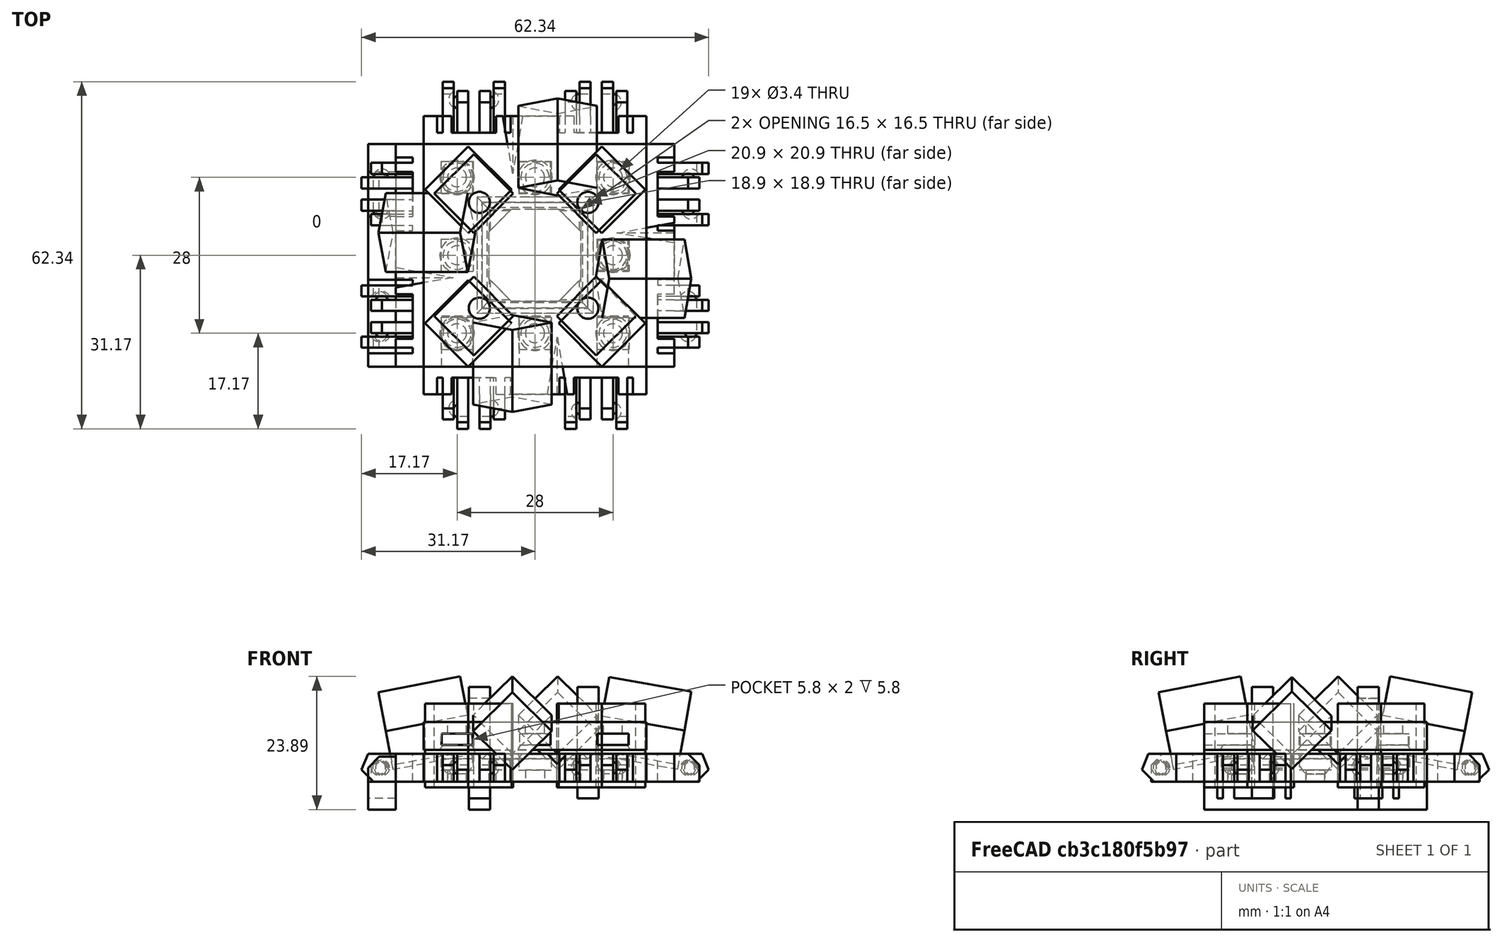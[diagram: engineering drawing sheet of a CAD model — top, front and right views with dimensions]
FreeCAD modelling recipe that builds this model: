
FCSTD DOCUMENT  (FreeCAD 0.17R13522 (Git))
Label: Robot Plates 0.5
License: All rights reserved
LicenseURL: http://en.wikipedia.org/wiki/All_rights_reserved
objects: Part::Box×264, Part::Cut×89, Part::Sphere×83, Part::MultiFuse×64, Part::Fuse×29, Part::Cylinder×27, Part::Chamfer×11, App::DocumentObjectGroup×2, Drawing::FeatureViewAnnotation×2, Drawing::FeaturePage×1
note: 567 computed .brp shape members not serialized (recipe doc carries the construction recipe); baked Part::Feature solids carry a one-line shape summary decoded from their .brp

FEATURE [Part::Box] Box  label="Cube"
  AttacherType = Attacher::AttachEngine3D
  Height = 5
  Length = 40
  Placement = pos=(0,0,-2) rot=(0,0,1;0rad)
  Width = 40
FEATURE [Part::Sphere] Sphere003  label="Mag Hole 3"
  Angle1 = -90
  Angle2 = 90
  Angle3 = 360
  AttacherType = Attacher::AttachEngine3D
  Placement = pos=(6,34,1.7) rot=(0,0,1;0rad)
  Radius = 2.85
FEATURE [Part::Sphere] Sphere005  label="Mag Hole 2"
  Angle1 = -90
  Angle2 = 90
  Angle3 = 360
  AttacherType = Attacher::AttachEngine3D
  Placement = pos=(34,20,1.7) rot=(0,0,1;0rad)
  Radius = 2.85
FEATURE [Part::Sphere] Sphere  label="Mag Hole"
  Angle1 = -90
  Angle2 = 90
  Angle3 = 360
  AttacherType = Attacher::AttachEngine3D
  Placement = pos=(6,6,1.7) rot=(0,0,1;0rad)
  Radius = 2.85
FEATURE [Part::MultiFuse] Fusion004
  Shapes = -> [Sphere,Sphere005,Sphere003]
FEATURE [Part::Cut] Cut003
  Base = -> Box
  Tool = -> Fusion004
FEATURE [Part::Box] Box001  label="Cube001"
  AttacherType = Attacher::AttachEngine3D
  Height = 7
  Length = 5
  Placement = pos=(-5,0,-2) rot=(0,0,1;0rad)
  Width = 40
FEATURE [Part::Box] Box002  label="Cube002"
  AttacherType = Attacher::AttachEngine3D
  Height = 7
  Length = 10
  Placement = pos=(-15,6,-2) rot=(0,0,1;0rad)
  Width = 2
FEATURE [Part::Box] Box003  label="Cube003"
  AttacherType = Attacher::AttachEngine3D
  Height = 7
  Length = 10
  Placement = pos=(-15,10,-2) rot=(0,0,1;0rad)
  Width = 2
FEATURE [Part::Box] Box004  label="Cube004"
  AttacherType = Attacher::AttachEngine3D
  Height = 7
  Length = 10
  Placement = pos=(-15,25.4,-2) rot=(0,0,1;0rad)
  Width = 2
FEATURE [Part::Box] Box005  label="Cube005"
  AttacherType = Attacher::AttachEngine3D
  Height = 7
  Length = 10
  Placement = pos=(-15,34.6,-2) rot=(0,0,1;0rad)
  Width = 2
FEATURE [Part::Sphere] Sphere008
  Angle1 = -90
  Angle2 = 90
  Angle3 = 360
  AttacherType = Attacher::AttachEngine3D
  Placement = pos=(-7.5,6.5,0.5) rot=(0,0,1;0rad)
  Radius = 1.25
FEATURE [Part::Box] Box006  label="Chamfer Cube"
  AttacherType = Attacher::AttachEngine3D
  Height = 10
  Length = 13
  Placement = pos=(-11.69,0,-1.19) rot=(0,-1,0;0.785398rad)
  Width = 40
FEATURE [Part::Sphere] Sphere009
  Angle1 = -90
  Angle2 = 90
  Angle3 = 360
  AttacherType = Attacher::AttachEngine3D
  Placement = pos=(-7.5,11.5,0.5) rot=(0,0,1;0rad)
  Radius = 1.25
FEATURE [Part::Sphere] Sphere010
  Angle1 = -90
  Angle2 = 90
  Angle3 = 360
  AttacherType = Attacher::AttachEngine3D
  Placement = pos=(-7.5,28,0.5) rot=(0,0,1;0rad)
  Radius = 1.5
FEATURE [Part::Sphere] Sphere011
  Angle1 = -90
  Angle2 = 90
  Angle3 = 360
  AttacherType = Attacher::AttachEngine3D
  Placement = pos=(-7.5,34,0.5) rot=(0,0,1;0rad)
  Radius = 1.5
FEATURE [Part::Box] Box007  label="Cube007"
  AttacherType = Attacher::AttachEngine3D
  Height = 7
  Length = 4
  Placement = pos=(-6,5,-2) rot=(0,0,1;0rad)
  Width = 1
FEATURE [Part::Box] Box008  label="Cube008"
  AttacherType = Attacher::AttachEngine3D
  Height = 7
  Length = 4
  Placement = pos=(-6,8,-2) rot=(0,0,1;0rad)
  Width = 2
FEATURE [Part::Box] Box009  label="Cube009"
  AttacherType = Attacher::AttachEngine3D
  Height = 7
  Length = 4
  Placement = pos=(-6,12,-2) rot=(0,0,1;0rad)
  Width = 1
FEATURE [Part::Box] Box010  label="Cube010"
  AttacherType = Attacher::AttachEngine3D
  Height = 7
  Length = 4
  Placement = pos=(-6,24.4,-2) rot=(0,0,1;0rad)
  Width = 1
FEATURE [Part::Box] Box011  label="Cube011"
  AttacherType = Attacher::AttachEngine3D
  Height = 7
  Length = 4
  Placement = pos=(-6,36.6,-2) rot=(0,0,1;0rad)
  Width = 1
FEATURE [Part::Box] Box012  label="Cube012"
  AttacherType = Attacher::AttachEngine3D
  Height = 7
  Length = 4
  Placement = pos=(-6,27.4,-2) rot=(0,0,1;0rad)
  Width = 7.2
FEATURE [Part::MultiFuse] Fusion003  label="Extra Holes for Clips"
  Shapes = -> [Box012,Box009,Box011,Box008,Box010,Box007]
FEATURE [Part::Box] Box013  label="Re-level Edge Clip Block"
  AttacherType = Attacher::AttachEngine3D
  Height = 10
  Length = 20
  Placement = pos=(-19,-2,3) rot=(0,0,1;0rad)
  Width = 44
FEATURE [Part::Box] Box014  label="Cube014"
  AttacherType = Attacher::AttachEngine3D
  Height = 7
  Length = 10
  Placement = pos=(-10,34.6,0) rot=(0,0,1;0rad)
  Width = 2
FEATURE [Part::Box] Box015  label="Cube015"
  AttacherType = Attacher::AttachEngine3D
  Height = 7
  Length = 5
  Width = 40
FEATURE [Part::Box] Box016  label="Cube016"
  AttacherType = Attacher::AttachEngine3D
  Height = 7
  Length = 10
  Placement = pos=(-10,25.4,0) rot=(0,0,1;0rad)
  Width = 2
FEATURE [Part::Box] Box017  label="Cube017"
  AttacherType = Attacher::AttachEngine3D
  Height = 7
  Length = 10
  Placement = pos=(-10,10,0) rot=(0,0,1;0rad)
  Width = 2
FEATURE [Part::Box] Box018  label="Cube018"
  AttacherType = Attacher::AttachEngine3D
  Height = 7
  Length = 10
  Placement = pos=(-10,6,0) rot=(0,0,1;0rad)
  Width = 2
FEATURE [Part::Sphere] Sphere012
  Angle1 = -90
  Angle2 = 90
  Angle3 = 360
  AttacherType = Attacher::AttachEngine3D
  Placement = pos=(-3,6.5,2.5) rot=(0,0,1;0rad)
  Radius = 1.25
FEATURE [Part::Box] Box019  label="Cube019"
  AttacherType = Attacher::AttachEngine3D
  Height = 10
  Length = 13
  Placement = pos=(-10.19,0,-1.19) rot=(0,-1,0;0.785398rad)
  Width = 40
FEATURE [Part::Sphere] Sphere013
  Angle1 = -90
  Angle2 = 90
  Angle3 = 360
  AttacherType = Attacher::AttachEngine3D
  Placement = pos=(-3,11.5,2.5) rot=(0,0,1;0rad)
  Radius = 1.25
FEATURE [Part::Sphere] Sphere014
  Angle1 = -90
  Angle2 = 90
  Angle3 = 360
  AttacherType = Attacher::AttachEngine3D
  Placement = pos=(-3,28,2.5) rot=(0,0,1;0rad)
  Radius = 1.5
FEATURE [Part::Sphere] Sphere015
  Angle1 = -90
  Angle2 = 90
  Angle3 = 360
  AttacherType = Attacher::AttachEngine3D
  Placement = pos=(-3,34,2.5) rot=(0,0,1;0rad)
  Radius = 1.5
FEATURE [Part::MultiFuse] Fusion005
  Shapes = -> [Box015,Box018,Box017,Box016,Box014]
FEATURE [Part::Cut] Cut005
  Base = -> Fusion005
  Tool = -> Box019
FEATURE [Part::MultiFuse] Fusion006
  Shapes = -> [Sphere012,Sphere013,Cut005]
FEATURE [Part::MultiFuse] Fusion007
  Shapes = -> [Sphere015,Sphere014]
FEATURE [Part::Cut] Cut006
  Base = -> Fusion006
  Tool = -> Fusion007
FEATURE [Part::Chamfer] Chamfer002
  Base = -> Cut006
  Edges = 4 edges r=4: [Edge31,Edge37,Edge43,Edge46]
FEATURE [Part::Box] Box020  label="Cube020"
  AttacherType = Attacher::AttachEngine3D
  Height = 7
  Length = 4
  Placement = pos=(-1,5,0) rot=(0,0,1;0rad)
  Width = 1
FEATURE [Part::Box] Box021  label="Cube021"
  AttacherType = Attacher::AttachEngine3D
  Height = 7
  Length = 4
  Placement = pos=(-1,8,0) rot=(0,0,1;0rad)
  Width = 2
FEATURE [Part::Box] Box022  label="Cube022"
  AttacherType = Attacher::AttachEngine3D
  Height = 7
  Length = 4
  Placement = pos=(-1,12,0) rot=(0,0,1;0rad)
  Width = 1
FEATURE [Part::Box] Box023  label="Cube023"
  AttacherType = Attacher::AttachEngine3D
  Height = 7
  Length = 4
  Placement = pos=(-1,24.4,0) rot=(0,0,1;0rad)
  Width = 1
FEATURE [Part::Box] Box024  label="Cube024"
  AttacherType = Attacher::AttachEngine3D
  Height = 7
  Length = 4
  Placement = pos=(-1,36.6,0) rot=(0,0,1;0rad)
  Width = 1
FEATURE [Part::Box] Box025  label="Cube025"
  AttacherType = Attacher::AttachEngine3D
  Height = 7
  Length = 4
  Placement = pos=(-1,27.4,0) rot=(0,0,1;0rad)
  Width = 7.2
FEATURE [Part::MultiFuse] Fusion008
  Shapes = -> [Box025,Box022,Box024,Box021,Box023,Box020]
FEATURE [Part::Cut] Cut007
  Base = -> Chamfer002
  Placement = pos=(-5,40,3) rot=(1,0,0;3.14159rad)
  Tool = -> Fusion008
FEATURE [Part::Box] Box026  label="Cube026"
  AttacherType = Attacher::AttachEngine3D
  Height = 10
  Length = 12
  Placement = pos=(-11,-2,-12) rot=(0,0,1;0rad)
  Width = 44
FEATURE [Part::Cut] Cut008
  Base = -> Cut007
  Placement = pos=(40,0,0) rot=(0,0,1;1.5708rad)
  Tool = -> Box026
FEATURE [Part::Box] Box027  label="Cube027"
  AttacherType = Attacher::AttachEngine3D
  Height = 7
  Length = 4
  Placement = pos=(-1,12,0) rot=(0,0,1;0rad)
  Width = 1
FEATURE [Part::Box] Box028  label="Cube028"
  AttacherType = Attacher::AttachEngine3D
  Height = 10
  Length = 13
  Placement = pos=(-10.19,0,-1.19) rot=(0,-1,0;0.785398rad)
  Width = 40
FEATURE [Part::Box] Box029  label="Cube029"
  AttacherType = Attacher::AttachEngine3D
  Height = 7
  Length = 4
  Placement = pos=(-1,27.4,0) rot=(0,0,1;0rad)
  Width = 7.2
FEATURE [Part::Box] Box030  label="Cube030"
  AttacherType = Attacher::AttachEngine3D
  Height = 7
  Length = 4
  Placement = pos=(-1,5,0) rot=(0,0,1;0rad)
  Width = 1
FEATURE [Part::Box] Box031  label="Cube031"
  AttacherType = Attacher::AttachEngine3D
  Height = 7
  Length = 10
  Placement = pos=(-10,6,0) rot=(0,0,1;0rad)
  Width = 2
FEATURE [Part::Box] Box032  label="Cube032"
  AttacherType = Attacher::AttachEngine3D
  Height = 10
  Length = 12
  Placement = pos=(-11,-2,-12) rot=(0,0,1;0rad)
  Width = 44
FEATURE [Part::Sphere] Sphere016
  Angle1 = -90
  Angle2 = 90
  Angle3 = 360
  AttacherType = Attacher::AttachEngine3D
  Placement = pos=(-3,6.5,2.5) rot=(0,0,1;0rad)
  Radius = 1.25
FEATURE [Part::Box] Box033  label="Cube033"
  AttacherType = Attacher::AttachEngine3D
  Height = 7
  Length = 10
  Placement = pos=(-10,25.4,0) rot=(0,0,1;0rad)
  Width = 2
FEATURE [Part::Box] Box034  label="Cube034"
  AttacherType = Attacher::AttachEngine3D
  Height = 7
  Length = 10
  Placement = pos=(-10,10,0) rot=(0,0,1;0rad)
  Width = 2
FEATURE [Part::Sphere] Sphere017
  Angle1 = -90
  Angle2 = 90
  Angle3 = 360
  AttacherType = Attacher::AttachEngine3D
  Placement = pos=(-3,28,2.5) rot=(0,0,1;0rad)
  Radius = 1.5
FEATURE [Part::Sphere] Sphere018
  Angle1 = -90
  Angle2 = 90
  Angle3 = 360
  AttacherType = Attacher::AttachEngine3D
  Placement = pos=(-3,11.5,2.5) rot=(0,0,1;0rad)
  Radius = 1.25
FEATURE [Part::Box] Box035  label="Cube035"
  AttacherType = Attacher::AttachEngine3D
  Height = 7
  Length = 4
  Placement = pos=(-1,36.6,0) rot=(0,0,1;0rad)
  Width = 1
FEATURE [Part::Sphere] Sphere019
  Angle1 = -90
  Angle2 = 90
  Angle3 = 360
  AttacherType = Attacher::AttachEngine3D
  Placement = pos=(-3,34,2.5) rot=(0,0,1;0rad)
  Radius = 1.5
FEATURE [Part::MultiFuse] Fusion011
  Shapes = -> [Sphere019,Sphere017]
FEATURE [Part::Box] Box036  label="Cube036"
  AttacherType = Attacher::AttachEngine3D
  Height = 7
  Length = 4
  Placement = pos=(-1,8,0) rot=(0,0,1;0rad)
  Width = 2
FEATURE [Part::Box] Box037  label="Cube037"
  AttacherType = Attacher::AttachEngine3D
  Height = 7
  Length = 10
  Placement = pos=(-10,34.6,0) rot=(0,0,1;0rad)
  Width = 2
FEATURE [Part::Box] Box038  label="Cube038"
  AttacherType = Attacher::AttachEngine3D
  Height = 7
  Length = 4
  Placement = pos=(-1,24.4,0) rot=(0,0,1;0rad)
  Width = 1
FEATURE [Part::MultiFuse] Fusion009
  Shapes = -> [Box029,Box027,Box035,Box036,Box038,Box030]
FEATURE [Part::Box] Box039  label="Cube039"
  AttacherType = Attacher::AttachEngine3D
  Height = 7
  Length = 5
  Width = 40
FEATURE [Part::MultiFuse] Fusion012
  Shapes = -> [Box039,Box031,Box034,Box033,Box037]
FEATURE [Part::Cut] Cut011
  Base = -> Fusion012
  Tool = -> Box028
FEATURE [Part::MultiFuse] Fusion010
  Shapes = -> [Sphere016,Sphere018,Cut011]
FEATURE [Part::Cut] Cut012
  Base = -> Fusion010
  Tool = -> Fusion011
FEATURE [Part::Chamfer] Chamfer003
  Base = -> Cut012
  Edges = 4 edges r=4: [Edge31,Edge37,Edge43,Edge46]
FEATURE [Part::Cut] Cut010
  Base = -> Chamfer003
  Placement = pos=(-5,40,3) rot=(1,0,0;3.14159rad)
  Tool = -> Fusion009
FEATURE [Part::Cut] Cut009
  Base = -> Cut010
  Placement = pos=(40,40,0) rot=(0,0,1;3.14159rad)
  Tool = -> Box032
FEATURE [Part::Sphere] Sphere020
  Angle1 = -90
  Angle2 = 90
  Angle3 = 360
  AttacherType = Attacher::AttachEngine3D
  Placement = pos=(-3,11.5,2.5) rot=(0,0,1;0rad)
  Radius = 1.25
FEATURE [Part::Box] Box040  label="Cube040"
  AttacherType = Attacher::AttachEngine3D
  Height = 7
  Length = 10
  Placement = pos=(-10,6,0) rot=(0,0,1;0rad)
  Width = 2
FEATURE [Part::Box] Box041  label="Cube041"
  AttacherType = Attacher::AttachEngine3D
  Height = 7
  Length = 4
  Placement = pos=(-1,8,0) rot=(0,0,1;0rad)
  Width = 2
FEATURE [Part::Box] Box042  label="Cube042"
  AttacherType = Attacher::AttachEngine3D
  Height = 7
  Length = 10
  Placement = pos=(-10,10,0) rot=(0,0,1;0rad)
  Width = 2
FEATURE [Part::Box] Box043  label="Cube043"
  AttacherType = Attacher::AttachEngine3D
  Height = 10
  Length = 12
  Placement = pos=(-11,-2,-12) rot=(0,0,1;0rad)
  Width = 44
FEATURE [Part::Box] Box044  label="Cube044"
  AttacherType = Attacher::AttachEngine3D
  Height = 7
  Length = 4
  Placement = pos=(-1,5,0) rot=(0,0,1;0rad)
  Width = 1
FEATURE [Part::Sphere] Sphere021
  Angle1 = -90
  Angle2 = 90
  Angle3 = 360
  AttacherType = Attacher::AttachEngine3D
  Placement = pos=(-3,28,2.5) rot=(0,0,1;0rad)
  Radius = 1.5
FEATURE [Part::Sphere] Sphere022
  Angle1 = -90
  Angle2 = 90
  Angle3 = 360
  AttacherType = Attacher::AttachEngine3D
  Placement = pos=(-3,6.5,2.5) rot=(0,0,1;0rad)
  Radius = 1.25
FEATURE [Part::Sphere] Sphere023
  Angle1 = -90
  Angle2 = 90
  Angle3 = 360
  AttacherType = Attacher::AttachEngine3D
  Placement = pos=(-3,34,2.5) rot=(0,0,1;0rad)
  Radius = 1.5
FEATURE [Part::Box] Box045  label="Cube045"
  AttacherType = Attacher::AttachEngine3D
  Height = 7
  Length = 4
  Placement = pos=(-1,12,0) rot=(0,0,1;0rad)
  Width = 1
FEATURE [Part::Box] Box046  label="Cube046"
  AttacherType = Attacher::AttachEngine3D
  Height = 7
  Length = 5
  Width = 40
FEATURE [Part::Box] Box047  label="Cube047"
  AttacherType = Attacher::AttachEngine3D
  Height = 7
  Length = 4
  Placement = pos=(-1,36.6,0) rot=(0,0,1;0rad)
  Width = 1
FEATURE [Part::Box] Box048  label="Cube048"
  AttacherType = Attacher::AttachEngine3D
  Height = 7
  Length = 4
  Placement = pos=(-1,24.4,0) rot=(0,0,1;0rad)
  Width = 1
FEATURE [Part::Box] Box049  label="Cube049"
  AttacherType = Attacher::AttachEngine3D
  Height = 7
  Length = 10
  Placement = pos=(-10,25.4,0) rot=(0,0,1;0rad)
  Width = 2
FEATURE [Part::Box] Box050  label="Cube050"
  AttacherType = Attacher::AttachEngine3D
  Height = 10
  Length = 13
  Placement = pos=(-10.19,0,-1.19) rot=(0,-1,0;0.785398rad)
  Width = 40
FEATURE [Part::Box] Box051  label="Cube051"
  AttacherType = Attacher::AttachEngine3D
  Height = 7
  Length = 10
  Placement = pos=(-10,34.6,0) rot=(0,0,1;0rad)
  Width = 2
FEATURE [Part::MultiFuse] Fusion015
  Shapes = -> [Box046,Box040,Box042,Box049,Box051]
FEATURE [Part::Cut] Cut013
  Base = -> Fusion015
  Tool = -> Box050
FEATURE [Part::MultiFuse] Fusion013
  Shapes = -> [Sphere022,Sphere020,Cut013]
FEATURE [Part::MultiFuse] Fusion016
  Shapes = -> [Sphere023,Sphere021]
FEATURE [Part::Cut] Cut014
  Base = -> Fusion013
  Tool = -> Fusion016
FEATURE [Part::Chamfer] Chamfer004
  Base = -> Cut014
  Edges = 4 edges r=4: [Edge31,Edge37,Edge43,Edge46]
FEATURE [Part::Box] Box052  label="Cube052"
  AttacherType = Attacher::AttachEngine3D
  Height = 7
  Length = 4
  Placement = pos=(-1,27.4,0) rot=(0,0,1;0rad)
  Width = 7.2
FEATURE [Part::MultiFuse] Fusion014
  Shapes = -> [Box052,Box045,Box047,Box041,Box048,Box044]
FEATURE [Part::Cut] Cut016
  Base = -> Chamfer004
  Placement = pos=(-5,40,3) rot=(1,0,0;3.14159rad)
  Tool = -> Fusion014
FEATURE [Part::Cut] Cut015
  Base = -> Cut016
  Placement = pos=(0,40,0) rot=(0,0,-1;1.5708rad)
  Tool = -> Box043
FEATURE [Part::Box] Box054  label="Cube054"
  AttacherType = Attacher::AttachEngine3D
  Height = 15
  Length = 10
  Placement = pos=(9,2,-3) rot=(0,0,1;0.785398rad)
  Width = 10
FEATURE [Part::Box] Box055  label="Cube055"
  AttacherType = Attacher::AttachEngine3D
  Height = 15
  Length = 10
  Placement = pos=(31,24,-3) rot=(0,0,1;0.785398rad)
  Width = 10
FEATURE [Part::Box] Box056  label="Cube056"
  AttacherType = Attacher::AttachEngine3D
  Height = 15
  Length = 10
  Placement = pos=(31,2,-3) rot=(0,0,1;0.785398rad)
  Width = 10
FEATURE [Part::Box] Box057  label="Cube057"
  AttacherType = Attacher::AttachEngine3D
  Height = 15
  Length = 10
  Placement = pos=(9,24,-3) rot=(0,0,1;0.785398rad)
  Width = 10
FEATURE [Part::MultiFuse] Fusion017
  Shapes = -> [Box054,Box057,Box056,Box055]
FEATURE [Part::Box] Box058  label="Cube058"
  AttacherType = Attacher::AttachEngine3D
  Height = 5
  Length = 40
  Placement = pos=(0,0,3.7) rot=(0,0,1;0rad)
  Width = 40
FEATURE [Part::Box] Box059  label="Square Nut Hole 008"
  AttacherType = Attacher::AttachEngine3D
  Height = 2
  Length = 5.6
  Placement = pos=(17.2,31.2,4.6) rot=(0,0,1;0rad)
  Width = 5.6
FEATURE [Part::Box] Box060  label="Square Nut Hole 009"
  AttacherType = Attacher::AttachEngine3D
  Height = 2
  Length = 5.6
  Placement = pos=(17.2,-0.85,4.6) rot=(0,0,1;0rad)
  Width = 10
FEATURE [Part::Box] Box061  label="Square Nut Hole 010"
  AttacherType = Attacher::AttachEngine3D
  Height = 2
  Length = 5.6
  Placement = pos=(31.2,-0.85,4.6) rot=(0,0,1;0rad)
  Width = 10
FEATURE [Part::Box] Box062  label="Square Nut Hole 011"
  AttacherType = Attacher::AttachEngine3D
  Height = 2
  Length = 5.4
  Placement = pos=(31.3,17.3,4.6) rot=(0,0,1;0rad)
  Width = 5.4
FEATURE [Part::Box] Box063  label="Square Nut Hole 012"
  AttacherType = Attacher::AttachEngine3D
  Height = 2
  Length = 5.7
  Placement = pos=(3.15,31.15,4.6) rot=(0,0,1;0rad)
  Width = 5.7
FEATURE [Part::Box] Box064  label="Square Nut Hole 013"
  AttacherType = Attacher::AttachEngine3D
  Height = 2
  Length = 5.5
  Placement = pos=(31.25,31.25,4.6) rot=(0,0,1;0rad)
  Width = 5.5
FEATURE [Part::Box] Box065  label="Square Nut Hole 014"
  AttacherType = Attacher::AttachEngine3D
  Height = 2
  Length = 5.8
  Placement = pos=(3.1,17.1,4.6) rot=(0,0,1;0rad)
  Width = 5.8
FEATURE [Part::Box] Box066  label="Square Nut Hole 015"
  AttacherType = Attacher::AttachEngine3D
  Height = 2
  Length = 5.6
  Placement = pos=(3.2,-0.85,4.6) rot=(0,0,1;0rad)
  Width = 10
FEATURE [Part::Sphere] Sphere006  label="Nut Clearence1"
  Angle1 = -90
  Angle2 = 90
  Angle3 = 360
  AttacherType = Attacher::AttachEngine3D
  Placement = pos=(6,6,2.4) rot=(0,0,1;0rad)
  Radius = 3.35
FEATURE [Part::Sphere] Sphere024
  Angle1 = -90
  Angle2 = 90
  Angle3 = 360
  AttacherType = Attacher::AttachEngine3D
  Placement = pos=(6,34,2.4) rot=(0,0,1;0rad)
  Radius = 3.35
FEATURE [Part::Sphere] Sphere007
  Angle1 = -90
  Angle2 = 90
  Angle3 = 360
  AttacherType = Attacher::AttachEngine3D
  Placement = pos=(34,20,2.4) rot=(0,0,1;0rad)
  Radius = 3.35
FEATURE [Part::Sphere] Sphere001
  Angle1 = -90
  Angle2 = 90
  Angle3 = 360
  AttacherType = Attacher::AttachEngine3D
  Placement = pos=(34,6,2.4) rot=(0,0,1;0rad)
  Radius = 3.35
FEATURE [Part::Sphere] Sphere025
  Angle1 = -90
  Angle2 = 90
  Angle3 = 360
  AttacherType = Attacher::AttachEngine3D
  Placement = pos=(20,6,2.4) rot=(0,0,1;0rad)
  Radius = 3.35
FEATURE [Part::Sphere] Sphere026
  Angle1 = -90
  Angle2 = 90
  Angle3 = 360
  AttacherType = Attacher::AttachEngine3D
  Placement = pos=(20,34,2.4) rot=(0,0,1;0rad)
  Radius = 3.35
FEATURE [Part::Sphere] Sphere004
  Angle1 = -90
  Angle2 = 90
  Angle3 = 360
  AttacherType = Attacher::AttachEngine3D
  Placement = pos=(6,20,2.4) rot=(0,0,1;0rad)
  Radius = 3.35
FEATURE [Part::Sphere] Sphere002
  Angle1 = -90
  Angle2 = 90
  Angle3 = 360
  AttacherType = Attacher::AttachEngine3D
  Placement = pos=(34,34,2.4) rot=(0,0,1;0rad)
  Radius = 3.35
FEATURE [Part::Cylinder] Cylinder
  Angle = 360
  AttacherType = Attacher::AttachEngine3D
  Height = 10
  Placement = pos=(6,6,0) rot=(0,0,1;0rad)
  Radius = 1.7
FEATURE [Part::Cylinder] Cylinder002
  Angle = 360
  AttacherType = Attacher::AttachEngine3D
  Height = 10
  Placement = pos=(34,6,0) rot=(0,0,1;0rad)
  Radius = 1.7
FEATURE [Part::Cylinder] Cylinder001
  Angle = 360
  AttacherType = Attacher::AttachEngine3D
  Height = 10
  Placement = pos=(20,6,0) rot=(0,0,1;0rad)
  Radius = 1.7
FEATURE [Part::Cylinder] Cylinder003
  Angle = 360
  AttacherType = Attacher::AttachEngine3D
  Height = 10
  Placement = pos=(34,34,0) rot=(0,0,1;0rad)
  Radius = 1.7
FEATURE [Part::Cylinder] Cylinder004
  Angle = 360
  AttacherType = Attacher::AttachEngine3D
  Height = 10
  Placement = pos=(20,34,0) rot=(0,0,1;0rad)
  Radius = 1.7
FEATURE [Part::Cylinder] Cylinder005
  Angle = 360
  AttacherType = Attacher::AttachEngine3D
  Height = 10
  Placement = pos=(6,34,0) rot=(0,0,1;0rad)
  Radius = 1.7
FEATURE [Part::Cylinder] Cylinder006
  Angle = 360
  AttacherType = Attacher::AttachEngine3D
  Height = 10
  Placement = pos=(6,20,0) rot=(0,0,1;0rad)
  Radius = 1.7
FEATURE [Part::Cylinder] Cylinder007
  Angle = 360
  AttacherType = Attacher::AttachEngine3D
  Height = 10
  Placement = pos=(34,20,0) rot=(0,0,1;0rad)
  Radius = 1.7
FEATURE [Part::MultiFuse] Fusion018
  Shapes = -> [Cylinder,Cylinder004,Cylinder007,Cylinder005,Cylinder006,Cylinder001,Cylinder002,Cylinder003]
FEATURE [Part::MultiFuse] Fusion019
  Shapes = -> [Sphere007,Sphere024,Sphere006,Sphere025,Sphere001,Sphere026,Sphere004,Sphere002]
FEATURE [Part::MultiFuse] Fusion020
  Shapes = -> [Box061,Box065,Box062,Box063,Box064,Box066,Box059,Box060]
FEATURE [Part::Cut] Cut017
  Base = -> Box058
  Tool = -> Fusion020
FEATURE [Part::Cut] Cut019
  Base = -> Cut017
  Tool = -> Fusion019
FEATURE [Part::Cut] Cut018
  Base = -> Cut019
  Tool = -> Fusion018
FEATURE [Part::Cylinder] Cylinder008
  Angle = 360
  AttacherType = Attacher::AttachEngine3D
  Height = 20
  Placement = pos=(10,10.5,-5) rot=(0,0,1;0rad)
  Radius = 1.9
FEATURE [Part::Cylinder] Cylinder009
  Angle = 360
  AttacherType = Attacher::AttachEngine3D
  Height = 20
  Placement = pos=(29.5,10.5,-5) rot=(0,0,1;0rad)
  Radius = 1.9
FEATURE [Part::Cylinder] Cylinder010
  Angle = 360
  AttacherType = Attacher::AttachEngine3D
  Height = 20
  Placement = pos=(29.5,29.5,-5) rot=(0,0,1;0rad)
  Radius = 1.9
FEATURE [Part::Cylinder] Cylinder011
  Angle = 360
  AttacherType = Attacher::AttachEngine3D
  Height = 20
  Placement = pos=(10,29.5,-7) rot=(0,0,1;0rad)
  Radius = 1.9
FEATURE [Part::MultiFuse] Fusion021  label="M2 Screw holes"
  Shapes = -> [Cylinder008,Cylinder009,Cylinder011,Cylinder010]
FEATURE [Part::Box] Box067  label="Square Nut Hole 016"
  AttacherType = Attacher::AttachEngine3D
  Height = 2
  Length = 5.8
  Placement = pos=(31.1,17.1,4.6) rot=(0,0,1;0rad)
  Width = 5.8
FEATURE [Part::Box] Box068  label="Square Nut Hole 017"
  AttacherType = Attacher::AttachEngine3D
  Height = 2
  Length = 5.8
  Placement = pos=(17.1,3.1,4.6) rot=(0,0,1;0rad)
  Width = 5.8
FEATURE [Part::Box] Box069  label="Square Nut Hole 018"
  AttacherType = Attacher::AttachEngine3D
  Height = 2
  Length = 5.8
  Placement = pos=(31.1,3.1,4.6) rot=(0,0,1;0rad)
  Width = 5.8
FEATURE [Part::Box] Box070  label="Square Nut Hole 019"
  AttacherType = Attacher::AttachEngine3D
  Height = 2
  Length = 5.8
  Placement = pos=(3.1,3.1,4.6) rot=(0,0,1;0rad)
  Width = 5.8
FEATURE [Part::Box] Box071  label="Square Nut Hole 020"
  AttacherType = Attacher::AttachEngine3D
  Height = 2
  Length = 5.8
  Placement = pos=(3.1,31.1,4.6) rot=(0,0,1;0rad)
  Width = 5.8
FEATURE [Part::Box] Box072  label="Square Nut Hole 021"
  AttacherType = Attacher::AttachEngine3D
  Height = 2
  Length = 5.8
  Placement = pos=(17.1,31.1,4.6) rot=(0,0,1;0rad)
  Width = 5.8
FEATURE [Part::Box] Box073  label="Square Nut Hole 022"
  AttacherType = Attacher::AttachEngine3D
  Height = 2
  Length = 5.8
  Placement = pos=(31.1,31.1,4.6) rot=(0,0,1;0rad)
  Width = 5.8
FEATURE [Part::Box] Box074  label="Square Nut Hole 023"
  AttacherType = Attacher::AttachEngine3D
  Height = 2
  Length = 5.8
  Placement = pos=(3.1,17.1,4.6) rot=(0,0,1;0rad)
  Width = 5.8
FEATURE [Part::Cylinder] Cylinder012
  Angle = 360
  AttacherType = Attacher::AttachEngine3D
  Height = 10
  Placement = pos=(6,6,0) rot=(0,0,1;0rad)
  Radius = 1.7
FEATURE [Part::Cylinder] Cylinder013
  Angle = 360
  AttacherType = Attacher::AttachEngine3D
  Height = 10
  Placement = pos=(34,34,0) rot=(0,0,1;0rad)
  Radius = 1.7
FEATURE [Part::Cylinder] Cylinder014
  Angle = 360
  AttacherType = Attacher::AttachEngine3D
  Height = 10
  Placement = pos=(20,34,0) rot=(0,0,1;0rad)
  Radius = 1.7
FEATURE [Part::Cylinder] Cylinder015
  Angle = 360
  AttacherType = Attacher::AttachEngine3D
  Height = 10
  Placement = pos=(6,34,0) rot=(0,0,1;0rad)
  Radius = 1.7
FEATURE [Part::Cylinder] Cylinder016
  Angle = 360
  AttacherType = Attacher::AttachEngine3D
  Height = 10
  Placement = pos=(6,20,0) rot=(0,0,1;0rad)
  Radius = 1.7
FEATURE [Part::Cylinder] Cylinder017
  Angle = 360
  AttacherType = Attacher::AttachEngine3D
  Height = 10
  Placement = pos=(34,20,0) rot=(0,0,1;0rad)
  Radius = 1.7
FEATURE [Part::Cylinder] Cylinder018
  Angle = 360
  AttacherType = Attacher::AttachEngine3D
  Height = 10
  Placement = pos=(34,6,0) rot=(0,0,1;0rad)
  Radius = 1.7
FEATURE [Part::Cylinder] Cylinder019
  Angle = 360
  AttacherType = Attacher::AttachEngine3D
  Height = 10
  Placement = pos=(20,6,0) rot=(0,0,1;0rad)
  Radius = 1.7
FEATURE [Part::Box] Box075  label="Cube059"
  AttacherType = Attacher::AttachEngine3D
  Height = 5
  Length = 40
  Placement = pos=(0,0,-2) rot=(0,0,1;0rad)
  Width = 40
FEATURE [Part::Sphere] Sphere027
  Angle1 = -90
  Angle2 = 90
  Angle3 = 360
  AttacherType = Attacher::AttachEngine3D
  Placement = pos=(34,20,2.4) rot=(0,0,1;0rad)
  Radius = 3.35
FEATURE [Part::Sphere] Sphere028  label="Nut Clearence002"
  Angle1 = -90
  Angle2 = 90
  Angle3 = 360
  AttacherType = Attacher::AttachEngine3D
  Placement = pos=(6,6,2.4) rot=(0,0,1;0rad)
  Radius = 3.35
FEATURE [Part::Sphere] Sphere029
  Angle1 = -90
  Angle2 = 90
  Angle3 = 360
  AttacherType = Attacher::AttachEngine3D
  Placement = pos=(34,34,2.4) rot=(0,0,1;0rad)
  Radius = 3.35
FEATURE [Part::Sphere] Sphere030
  Angle1 = -90
  Angle2 = 90
  Angle3 = 360
  AttacherType = Attacher::AttachEngine3D
  Placement = pos=(34,6,2.4) rot=(0,0,1;0rad)
  Radius = 3.35
FEATURE [Part::Sphere] Sphere031
  Angle1 = -90
  Angle2 = 90
  Angle3 = 360
  AttacherType = Attacher::AttachEngine3D
  Placement = pos=(20,6,2.4) rot=(0,0,1;0rad)
  Radius = 3.35
FEATURE [Part::Sphere] Sphere032
  Angle1 = -90
  Angle2 = 90
  Angle3 = 360
  AttacherType = Attacher::AttachEngine3D
  Placement = pos=(6,34,2.4) rot=(0,0,1;0rad)
  Radius = 3.35
FEATURE [Part::Sphere] Sphere033
  Angle1 = -90
  Angle2 = 90
  Angle3 = 360
  AttacherType = Attacher::AttachEngine3D
  Placement = pos=(6,20,2.4) rot=(0,0,1;0rad)
  Radius = 3.35
FEATURE [Part::Sphere] Sphere034
  Angle1 = -90
  Angle2 = 90
  Angle3 = 360
  AttacherType = Attacher::AttachEngine3D
  Placement = pos=(20,34,2.4) rot=(0,0,1;0rad)
  Radius = 3.35
FEATURE [Part::Box] Box076  label="Cube060"
  AttacherType = Attacher::AttachEngine3D
  Height = 15
  Length = 16.5
  Placement = pos=(11.75,11.75,-3) rot=(0,0,1;0rad)
  Width = 16.5
FEATURE [Part::Box] Box077  label="Cube061"
  AttacherType = Attacher::AttachEngine3D
  Height = 15
  Length = 11
  Placement = pos=(8,24,-3) rot=(0,0,1;0.785398rad)
  Width = 11
FEATURE [Part::Box] Box078  label="Cube062"
  AttacherType = Attacher::AttachEngine3D
  Height = 15
  Length = 11
  Placement = pos=(8,0,-3) rot=(0,0,1;0.785398rad)
  Width = 11
FEATURE [Part::Box] Box079  label="Cube063"
  AttacherType = Attacher::AttachEngine3D
  Height = 15
  Length = 11
  Placement = pos=(32,0,-3) rot=(0,0,1;0.785398rad)
  Width = 11
FEATURE [Part::Box] Box080  label="Cube064"
  AttacherType = Attacher::AttachEngine3D
  Height = 15
  Length = 11
  Placement = pos=(32,24,-3) rot=(0,0,1;0.785398rad)
  Width = 11
FEATURE [Part::MultiFuse] Fusion022
  Shapes = -> [Box078,Box077,Box079,Box080]
FEATURE [Part::Cylinder] Cylinder020
  Angle = 360
  AttacherType = Attacher::AttachEngine3D
  Height = 20
  Placement = pos=(29.5,10.5,-5) rot=(0,0,1;0rad)
  Radius = 1.9
FEATURE [Part::Cylinder] Cylinder021
  Angle = 360
  AttacherType = Attacher::AttachEngine3D
  Height = 20
  Placement = pos=(10,29.5,-7) rot=(0,0,1;0rad)
  Radius = 1.9
FEATURE [Part::Cylinder] Cylinder022
  Angle = 360
  AttacherType = Attacher::AttachEngine3D
  Height = 20
  Placement = pos=(10,10.5,-5) rot=(0,0,1;0rad)
  Radius = 1.9
FEATURE [Part::Cylinder] Cylinder023
  Angle = 360
  AttacherType = Attacher::AttachEngine3D
  Height = 20
  Placement = pos=(29.5,29.5,-5) rot=(0,0,1;0rad)
  Radius = 1.9
FEATURE [Part::MultiFuse] Fusion023  label="M2 Screw holes001"
  Shapes = -> [Cylinder022,Cylinder020,Cylinder021,Cylinder023]
FEATURE [Part::MultiFuse] Fusion024  label="Square Nut Hole"
  Shapes = -> [Box067,Box073,Box071,Box069,Box068,Box070,Box072,Box074]
FEATURE [Part::MultiFuse] Fusion025  label="Square Nut Screw Holes"
  Shapes = -> [Cylinder012,Cylinder018,Cylinder016,Cylinder015,Cylinder014,Cylinder013,Cylinder017,Cylinder019]
FEATURE [Part::MultiFuse] Fusion026  label="Nut Chamfers"
  Shapes = -> [Sphere027,Sphere028,Sphere029,Sphere031,Sphere032,Sphere033,Sphere034,Sphere030]
FEATURE [App::DocumentObjectGroup] Group  label="Cubes"
  Group = -> [Fusion017,Fusion022]
FEATURE [Part::Box] Box083  label="Cube067"
  AttacherType = Attacher::AttachEngine3D
  Height = 10
  Length = 21
  Placement = pos=(9.5,9.5,2.1) rot=(0,0,1;0rad)
  Width = 21
FEATURE [Part::Box] Box084  label="Cube068"
  AttacherType = Attacher::AttachEngine3D
  Height = 14
  Length = 17
  Placement = pos=(11.5,11.5,0) rot=(0,0,1;0rad)
  Width = 17
FEATURE [Part::Cut] Cut020
  Base = -> Box083
  Tool = -> Box084
FEATURE [Part::Chamfer] Chamfer007
  Base = -> Cut020
  Edges = 8 edges r=0.95: [Edge4,Edge5,Edge14,Edge16,Edge17,Edge18,Edge19,Edge20]
FEATURE [Part::Chamfer] Chamfer008
  Base = -> Box076
  Edges = 4 edges r=4: [Edge1,Edge3,Edge5,Edge7]
FEATURE [Part::Box] Box085  label="Cube069"
  AttacherType = Attacher::AttachEngine3D
  Height = 15
  Length = 16
  Placement = pos=(12,12,-13) rot=(0,0,1;0rad)
  Width = 16
FEATURE [Part::Box] Box086  label="Cube070"
  AttacherType = Attacher::AttachEngine3D
  Height = 10
  Length = 10
  Placement = pos=(24,-6,1) rot=(0.205904,-0.974848,-0.085288;0.803573rad)
  Width = 15
FEATURE [Part::Box] Box089  label="Cube073"
  AttacherType = Attacher::AttachEngine3D
  Height = 10
  Length = 10
  Placement = pos=(17,32.0919,9.95) rot=(-0.225436,0.969773,-0.093378;0.807337rad)
  Width = 15
FEATURE [Part::Box] Box090  label="Cube074"
  AttacherType = Attacher::AttachEngine3D
  Height = 10
  Length = 15
  Placement = pos=(30.8481,15.8,2.86019) rot=(0.974848,0.205904,-0.085288;0.803573rad)
  Width = 10
FEATURE [Part::Box] Box091  label="Cube075"
  AttacherType = Attacher::AttachEngine3D
  Height = 10
  Length = 10
  Placement = pos=(7.9081,17,9.95) rot=(-0.450607,0.280623,0.847469;1.65638rad)
  Width = 15
FEATURE [Part::Box] Box092  label="Cube076"
  AttacherType = Attacher::AttachEngine3D
  Height = 10
  Length = 10
  Placement = pos=(23,7.9081,9.95) rot=(-0.381178,-0.08861,0.920245;3.06822rad)
  Width = 15
FEATURE [Part::Box] Box093  label="Cube077"
  AttacherType = Attacher::AttachEngine3D
  Height = 7
  Length = 5
  Width = 40
FEATURE [Part::Box] Box094  label="Cube078"
  AttacherType = Attacher::AttachEngine3D
  Height = 7
  Length = 10
  Placement = pos=(-10,6,0) rot=(0,0,1;0rad)
  Width = 2
FEATURE [Part::Box] Box095  label="Cube079"
  AttacherType = Attacher::AttachEngine3D
  Height = 7
  Length = 10
  Placement = pos=(-10,10,0) rot=(0,0,1;0rad)
  Width = 2
FEATURE [Part::Box] Box096  label="Cube080"
  AttacherType = Attacher::AttachEngine3D
  Height = 7
  Length = 10
  Placement = pos=(-10,25.4,0) rot=(0,0,1;0rad)
  Width = 2
FEATURE [Part::Box] Box097  label="Cube081"
  AttacherType = Attacher::AttachEngine3D
  Height = 7
  Length = 10
  Placement = pos=(-10,34.6,0) rot=(0,0,1;0rad)
  Width = 2
FEATURE [Part::Sphere] Sphere035
  Angle1 = -90
  Angle2 = 90
  Angle3 = 360
  AttacherType = Attacher::AttachEngine3D
  Placement = pos=(-3,6.5,2.5) rot=(0,0,1;0rad)
  Radius = 1.25
FEATURE [Part::Box] Box098  label="Cube082"
  AttacherType = Attacher::AttachEngine3D
  Height = 10
  Length = 13
  Placement = pos=(-10.19,0,-1.19) rot=(0,-1,0;0.785398rad)
  Width = 40
FEATURE [Part::Sphere] Sphere036
  Angle1 = -90
  Angle2 = 90
  Angle3 = 360
  AttacherType = Attacher::AttachEngine3D
  Placement = pos=(-3,11.5,2.5) rot=(0,0,1;0rad)
  Radius = 1.25
FEATURE [Part::Sphere] Sphere037
  Angle1 = -90
  Angle2 = 90
  Angle3 = 360
  AttacherType = Attacher::AttachEngine3D
  Placement = pos=(-3,28,2.5) rot=(0,0,1;0rad)
  Radius = 1.5
FEATURE [Part::Sphere] Sphere038
  Angle1 = -90
  Angle2 = 90
  Angle3 = 360
  AttacherType = Attacher::AttachEngine3D
  Placement = pos=(-3,34,2.5) rot=(0,0,1;0rad)
  Radius = 1.5
FEATURE [Part::MultiFuse] Fusion030
  Shapes = -> [Box093,Box094,Box095,Box096,Box097]
FEATURE [Part::Cut] Cut025
  Base = -> Fusion030
  Tool = -> Box098
FEATURE [Part::MultiFuse] Fusion031
  Shapes = -> [Sphere035,Sphere036,Cut025]
FEATURE [Part::MultiFuse] Fusion032
  Shapes = -> [Sphere038,Sphere037]
FEATURE [Part::Cut] Cut026
  Base = -> Fusion031
  Tool = -> Fusion032
FEATURE [Part::Chamfer] Chamfer009
  Base = -> Cut026
  Edges = 4 edges r=4: [Edge31,Edge37,Edge43,Edge46]
FEATURE [Part::Box] Box099  label="Cube083"
  AttacherType = Attacher::AttachEngine3D
  Height = 7
  Length = 4
  Placement = pos=(-1,5,0) rot=(0,0,1;0rad)
  Width = 1
FEATURE [Part::Box] Box100  label="Cube084"
  AttacherType = Attacher::AttachEngine3D
  Height = 7
  Length = 4
  Placement = pos=(-1,8,0) rot=(0,0,1;0rad)
  Width = 2
FEATURE [Part::Box] Box101  label="Cube085"
  AttacherType = Attacher::AttachEngine3D
  Height = 7
  Length = 4
  Placement = pos=(-1,12,0) rot=(0,0,1;0rad)
  Width = 1
FEATURE [Part::Box] Box102  label="Cube086"
  AttacherType = Attacher::AttachEngine3D
  Height = 7
  Length = 4
  Placement = pos=(-1,24.4,0) rot=(0,0,1;0rad)
  Width = 1
FEATURE [Part::Box] Box103  label="Cube087"
  AttacherType = Attacher::AttachEngine3D
  Height = 7
  Length = 4
  Placement = pos=(-1,36.6,0) rot=(0,0,1;0rad)
  Width = 1
FEATURE [Part::Box] Box104  label="Cube088"
  AttacherType = Attacher::AttachEngine3D
  Height = 7
  Length = 4
  Placement = pos=(-1,27.4,0) rot=(0,0,1;0rad)
  Width = 7.2
FEATURE [Part::MultiFuse] Fusion033
  Shapes = -> [Box104,Box101,Box103,Box100,Box102,Box099]
FEATURE [Part::Cut] Cut027
  Base = -> Chamfer009
  Placement = pos=(-5,40,3) rot=(1,0,0;3.14159rad)
  Tool = -> Fusion033
FEATURE [Part::Box] Box105  label="Cube089"
  AttacherType = Attacher::AttachEngine3D
  Height = 10
  Length = 12
  Placement = pos=(-11,-2,-12) rot=(0,0,1;0rad)
  Width = 44
FEATURE [Part::Cut] Cut028
  Base = -> Cut027
  Tool = -> Box105
FEATURE [Part::Box] Box106  label="Cube090"
  AttacherType = Attacher::AttachEngine3D
  Height = 7
  Length = 10
  Placement = pos=(-10,34.6,0) rot=(0,0,1;0rad)
  Width = 2
FEATURE [Part::Box] Box107  label="Cube091"
  AttacherType = Attacher::AttachEngine3D
  Height = 7
  Length = 5
  Width = 40
FEATURE [Part::Box] Box108  label="Cube092"
  AttacherType = Attacher::AttachEngine3D
  Height = 7
  Length = 10
  Placement = pos=(-10,25.4,0) rot=(0,0,1;0rad)
  Width = 2
FEATURE [Part::Box] Box109  label="Cube093"
  AttacherType = Attacher::AttachEngine3D
  Height = 7
  Length = 10
  Placement = pos=(-10,10,0) rot=(0,0,1;0rad)
  Width = 2
FEATURE [Part::Box] Box110  label="Cube094"
  AttacherType = Attacher::AttachEngine3D
  Height = 7
  Length = 10
  Placement = pos=(-10,6,0) rot=(0,0,1;0rad)
  Width = 2
FEATURE [Part::Sphere] Sphere039
  Angle1 = -90
  Angle2 = 90
  Angle3 = 360
  AttacherType = Attacher::AttachEngine3D
  Placement = pos=(-3,6.5,2.5) rot=(0,0,1;0rad)
  Radius = 1.25
FEATURE [Part::Box] Box111  label="Cube095"
  AttacherType = Attacher::AttachEngine3D
  Height = 10
  Length = 13
  Placement = pos=(-10.19,0,-1.19) rot=(0,-1,0;0.785398rad)
  Width = 40
FEATURE [Part::Sphere] Sphere040
  Angle1 = -90
  Angle2 = 90
  Angle3 = 360
  AttacherType = Attacher::AttachEngine3D
  Placement = pos=(-3,11.5,2.5) rot=(0,0,1;0rad)
  Radius = 1.25
FEATURE [Part::Sphere] Sphere041
  Angle1 = -90
  Angle2 = 90
  Angle3 = 360
  AttacherType = Attacher::AttachEngine3D
  Placement = pos=(-3,28,2.5) rot=(0,0,1;0rad)
  Radius = 1.5
FEATURE [Part::Sphere] Sphere042
  Angle1 = -90
  Angle2 = 90
  Angle3 = 360
  AttacherType = Attacher::AttachEngine3D
  Placement = pos=(-3,34,2.5) rot=(0,0,1;0rad)
  Radius = 1.5
FEATURE [Part::MultiFuse] Fusion034
  Shapes = -> [Box107,Box110,Box109,Box108,Box106]
FEATURE [Part::Cut] Cut029
  Base = -> Fusion034
  Tool = -> Box111
FEATURE [Part::MultiFuse] Fusion035
  Shapes = -> [Sphere039,Sphere040,Cut029]
FEATURE [Part::MultiFuse] Fusion036
  Shapes = -> [Sphere042,Sphere041]
FEATURE [Part::Cut] Cut030
  Base = -> Fusion035
  Tool = -> Fusion036
FEATURE [Part::Chamfer] Chamfer010
  Base = -> Cut030
  Edges = 4 edges r=4: [Edge31,Edge37,Edge43,Edge46]
FEATURE [Part::Box] Box112  label="Cube096"
  AttacherType = Attacher::AttachEngine3D
  Height = 7
  Length = 4
  Placement = pos=(-1,5,0) rot=(0,0,1;0rad)
  Width = 1
FEATURE [Part::Box] Box113  label="Cube097"
  AttacherType = Attacher::AttachEngine3D
  Height = 7
  Length = 4
  Placement = pos=(-1,8,0) rot=(0,0,1;0rad)
  Width = 2
FEATURE [Part::Box] Box114  label="Cube098"
  AttacherType = Attacher::AttachEngine3D
  Height = 7
  Length = 4
  Placement = pos=(-1,12,0) rot=(0,0,1;0rad)
  Width = 1
FEATURE [Part::Box] Box115  label="Cube099"
  AttacherType = Attacher::AttachEngine3D
  Height = 7
  Length = 4
  Placement = pos=(-1,24.4,0) rot=(0,0,1;0rad)
  Width = 1
FEATURE [Part::Box] Box116  label="Cube100"
  AttacherType = Attacher::AttachEngine3D
  Height = 7
  Length = 4
  Placement = pos=(-1,36.6,0) rot=(0,0,1;0rad)
  Width = 1
FEATURE [Part::Box] Box117  label="Cube101"
  AttacherType = Attacher::AttachEngine3D
  Height = 7
  Length = 4
  Placement = pos=(-1,27.4,0) rot=(0,0,1;0rad)
  Width = 7.2
FEATURE [Part::MultiFuse] Fusion037
  Shapes = -> [Box117,Box114,Box116,Box113,Box115,Box112]
FEATURE [Part::Cut] Cut031
  Base = -> Chamfer010
  Placement = pos=(-5,40,3) rot=(1,0,0;3.14159rad)
  Tool = -> Fusion037
FEATURE [Part::Box] Box118  label="Cube102"
  AttacherType = Attacher::AttachEngine3D
  Height = 10
  Length = 12
  Placement = pos=(-11,-2,-12) rot=(0,0,1;0rad)
  Width = 44
FEATURE [Part::Cut] Cut032
  Base = -> Cut031
  Placement = pos=(40,0,0) rot=(0,0,1;1.5708rad)
  Tool = -> Box118
FEATURE [Part::Box] Box119  label="Cube103"
  AttacherType = Attacher::AttachEngine3D
  Height = 7
  Length = 4
  Placement = pos=(-1,12,0) rot=(0,0,1;0rad)
  Width = 1
FEATURE [Part::Box] Box120  label="Cube104"
  AttacherType = Attacher::AttachEngine3D
  Height = 10
  Length = 13
  Placement = pos=(-10.19,0,-1.19) rot=(0,-1,0;0.785398rad)
  Width = 40
FEATURE [Part::Box] Box121  label="Cube105"
  AttacherType = Attacher::AttachEngine3D
  Height = 7
  Length = 4
  Placement = pos=(-1,27.4,0) rot=(0,0,1;0rad)
  Width = 7.2
FEATURE [Part::Box] Box122  label="Cube106"
  AttacherType = Attacher::AttachEngine3D
  Height = 7
  Length = 4
  Placement = pos=(-1,5,0) rot=(0,0,1;0rad)
  Width = 1
FEATURE [Part::Box] Box123  label="Cube107"
  AttacherType = Attacher::AttachEngine3D
  Height = 7
  Length = 10
  Placement = pos=(-10,6,0) rot=(0,0,1;0rad)
  Width = 2
FEATURE [Part::Box] Box124  label="Cube108"
  AttacherType = Attacher::AttachEngine3D
  Height = 10
  Length = 12
  Placement = pos=(-11,-2,-12) rot=(0,0,1;0rad)
  Width = 44
FEATURE [Part::Sphere] Sphere043
  Angle1 = -90
  Angle2 = 90
  Angle3 = 360
  AttacherType = Attacher::AttachEngine3D
  Placement = pos=(-3,6.5,2.5) rot=(0,0,1;0rad)
  Radius = 1.25
FEATURE [Part::Box] Box125  label="Cube109"
  AttacherType = Attacher::AttachEngine3D
  Height = 7
  Length = 10
  Placement = pos=(-10,25.4,0) rot=(0,0,1;0rad)
  Width = 2
FEATURE [Part::Box] Box126  label="Cube110"
  AttacherType = Attacher::AttachEngine3D
  Height = 7
  Length = 10
  Placement = pos=(-10,10,0) rot=(0,0,1;0rad)
  Width = 2
FEATURE [Part::Sphere] Sphere044
  Angle1 = -90
  Angle2 = 90
  Angle3 = 360
  AttacherType = Attacher::AttachEngine3D
  Placement = pos=(-3,28,2.5) rot=(0,0,1;0rad)
  Radius = 1.5
FEATURE [Part::Sphere] Sphere045
  Angle1 = -90
  Angle2 = 90
  Angle3 = 360
  AttacherType = Attacher::AttachEngine3D
  Placement = pos=(-3,11.5,2.5) rot=(0,0,1;0rad)
  Radius = 1.25
FEATURE [Part::Box] Box127  label="Cube111"
  AttacherType = Attacher::AttachEngine3D
  Height = 7
  Length = 4
  Placement = pos=(-1,36.6,0) rot=(0,0,1;0rad)
  Width = 1
FEATURE [Part::Sphere] Sphere046
  Angle1 = -90
  Angle2 = 90
  Angle3 = 360
  AttacherType = Attacher::AttachEngine3D
  Placement = pos=(-3,34,2.5) rot=(0,0,1;0rad)
  Radius = 1.5
FEATURE [Part::MultiFuse] Fusion040
  Shapes = -> [Sphere046,Sphere044]
FEATURE [Part::Box] Box128  label="Cube112"
  AttacherType = Attacher::AttachEngine3D
  Height = 7
  Length = 4
  Placement = pos=(-1,8,0) rot=(0,0,1;0rad)
  Width = 2
FEATURE [Part::Box] Box129  label="Cube113"
  AttacherType = Attacher::AttachEngine3D
  Height = 7
  Length = 10
  Placement = pos=(-10,34.6,0) rot=(0,0,1;0rad)
  Width = 2
FEATURE [Part::Box] Box130  label="Cube114"
  AttacherType = Attacher::AttachEngine3D
  Height = 7
  Length = 4
  Placement = pos=(-1,24.4,0) rot=(0,0,1;0rad)
  Width = 1
FEATURE [Part::MultiFuse] Fusion038
  Shapes = -> [Box121,Box119,Box127,Box128,Box130,Box122]
FEATURE [Part::Box] Box131  label="Cube115"
  AttacherType = Attacher::AttachEngine3D
  Height = 7
  Length = 5
  Width = 40
FEATURE [Part::MultiFuse] Fusion041
  Shapes = -> [Box131,Box123,Box126,Box125,Box129]
FEATURE [Part::Cut] Cut035
  Base = -> Fusion041
  Tool = -> Box120
FEATURE [Part::MultiFuse] Fusion039
  Shapes = -> [Sphere043,Sphere045,Cut035]
FEATURE [Part::Cut] Cut036
  Base = -> Fusion039
  Tool = -> Fusion040
FEATURE [Part::Chamfer] Chamfer011
  Base = -> Cut036
  Edges = 4 edges r=4: [Edge31,Edge37,Edge43,Edge46]
FEATURE [Part::Cut] Cut034
  Base = -> Chamfer011
  Placement = pos=(-5,40,3) rot=(1,0,0;3.14159rad)
  Tool = -> Fusion038
FEATURE [Part::Cut] Cut033
  Base = -> Cut034
  Placement = pos=(40,40,0) rot=(0,0,1;3.14159rad)
  Tool = -> Box124
FEATURE [Part::Sphere] Sphere047
  Angle1 = -90
  Angle2 = 90
  Angle3 = 360
  AttacherType = Attacher::AttachEngine3D
  Placement = pos=(-3,11.5,2.5) rot=(0,0,1;0rad)
  Radius = 1.25
FEATURE [Part::Box] Box132  label="Cube116"
  AttacherType = Attacher::AttachEngine3D
  Height = 7
  Length = 10
  Placement = pos=(-10,6,0) rot=(0,0,1;0rad)
  Width = 2
FEATURE [Part::Box] Box133  label="Cube117"
  AttacherType = Attacher::AttachEngine3D
  Height = 7
  Length = 4
  Placement = pos=(-1,8,0) rot=(0,0,1;0rad)
  Width = 2
FEATURE [Part::Box] Box134  label="Cube118"
  AttacherType = Attacher::AttachEngine3D
  Height = 7
  Length = 10
  Placement = pos=(-10,10,0) rot=(0,0,1;0rad)
  Width = 2
FEATURE [Part::Box] Box135  label="Cube119"
  AttacherType = Attacher::AttachEngine3D
  Height = 10
  Length = 12
  Placement = pos=(-11,-2,-12) rot=(0,0,1;0rad)
  Width = 44
FEATURE [Part::Box] Box136  label="Cube120"
  AttacherType = Attacher::AttachEngine3D
  Height = 7
  Length = 4
  Placement = pos=(-1,5,0) rot=(0,0,1;0rad)
  Width = 1
FEATURE [Part::Sphere] Sphere048
  Angle1 = -90
  Angle2 = 90
  Angle3 = 360
  AttacherType = Attacher::AttachEngine3D
  Placement = pos=(-3,28,2.5) rot=(0,0,1;0rad)
  Radius = 1.5
FEATURE [Part::Sphere] Sphere049
  Angle1 = -90
  Angle2 = 90
  Angle3 = 360
  AttacherType = Attacher::AttachEngine3D
  Placement = pos=(-3,6.5,2.5) rot=(0,0,1;0rad)
  Radius = 1.25
FEATURE [Part::Sphere] Sphere050
  Angle1 = -90
  Angle2 = 90
  Angle3 = 360
  AttacherType = Attacher::AttachEngine3D
  Placement = pos=(-3,34,2.5) rot=(0,0,1;0rad)
  Radius = 1.5
FEATURE [Part::Box] Box137  label="Cube121"
  AttacherType = Attacher::AttachEngine3D
  Height = 7
  Length = 4
  Placement = pos=(-1,12,0) rot=(0,0,1;0rad)
  Width = 1
FEATURE [Part::Box] Box138  label="Cube122"
  AttacherType = Attacher::AttachEngine3D
  Height = 7
  Length = 5
  Width = 40
FEATURE [Part::Box] Box139  label="Cube123"
  AttacherType = Attacher::AttachEngine3D
  Height = 7
  Length = 4
  Placement = pos=(-1,36.6,0) rot=(0,0,1;0rad)
  Width = 1
FEATURE [Part::Box] Box140  label="Cube124"
  AttacherType = Attacher::AttachEngine3D
  Height = 7
  Length = 4
  Placement = pos=(-1,24.4,0) rot=(0,0,1;0rad)
  Width = 1
FEATURE [Part::Box] Box141  label="Cube125"
  AttacherType = Attacher::AttachEngine3D
  Height = 7
  Length = 10
  Placement = pos=(-10,25.4,0) rot=(0,0,1;0rad)
  Width = 2
FEATURE [Part::Box] Box142  label="Cube126"
  AttacherType = Attacher::AttachEngine3D
  Height = 10
  Length = 13
  Placement = pos=(-10.19,0,-1.19) rot=(0,-1,0;0.785398rad)
  Width = 40
FEATURE [Part::Box] Box143  label="Cube127"
  AttacherType = Attacher::AttachEngine3D
  Height = 7
  Length = 10
  Placement = pos=(-10,34.6,0) rot=(0,0,1;0rad)
  Width = 2
FEATURE [Part::MultiFuse] Fusion044
  Shapes = -> [Box138,Box132,Box134,Box141,Box143]
FEATURE [Part::Cut] Cut037
  Base = -> Fusion044
  Tool = -> Box142
FEATURE [Part::MultiFuse] Fusion042
  Shapes = -> [Sphere049,Sphere047,Cut037]
FEATURE [Part::MultiFuse] Fusion045
  Shapes = -> [Sphere050,Sphere048]
FEATURE [Part::Cut] Cut038
  Base = -> Fusion042
  Tool = -> Fusion045
FEATURE [Part::Chamfer] Chamfer012
  Base = -> Cut038
  Edges = 4 edges r=4: [Edge31,Edge37,Edge43,Edge46]
FEATURE [Part::Box] Box144  label="Cube128"
  AttacherType = Attacher::AttachEngine3D
  Height = 7
  Length = 4
  Placement = pos=(-1,27.4,0) rot=(0,0,1;0rad)
  Width = 7.2
FEATURE [Part::MultiFuse] Fusion043
  Shapes = -> [Box144,Box137,Box139,Box133,Box140,Box136]
FEATURE [Part::Cut] Cut040
  Base = -> Chamfer012
  Placement = pos=(-5,40,3) rot=(1,0,0;3.14159rad)
  Tool = -> Fusion043
FEATURE [Part::Cut] Cut039
  Base = -> Cut040
  Placement = pos=(0,40,0) rot=(0,0,-1;1.5708rad)
  Tool = -> Box135
FEATURE [Part::MultiFuse] Fusion047
  Placement = pos=(0,40,6.7) rot=(1,0,0;3.14159rad)
  Shapes = -> [Fusion026,Fusion024,Fusion025]
FEATURE [Part::MultiFuse] Fusion048
  Shapes = -> [Box089,Box091,Box090,Box092]
FEATURE [Part::Box] Box145  label="Cube129"
  AttacherType = Attacher::AttachEngine3D
  Height = 15
  Length = 16
  Placement = pos=(12,12,-13) rot=(0,0,1;0rad)
  Width = 16
FEATURE [Part::Box] Box146  label="Cube130"
  AttacherType = Attacher::AttachEngine3D
  Height = 15
  Length = 16.5
  Placement = pos=(11.75,11.75,-3) rot=(0,0,1;0rad)
  Width = 16.5
FEATURE [Part::Chamfer] Chamfer013
  Base = -> Box146
  Edges = 4 edges r=4: [Edge1,Edge3,Edge5,Edge7]
FEATURE [Part::Box] Box147  label="Cube131"
  AttacherType = Attacher::AttachEngine3D
  Height = 10
  Length = 21
  Placement = pos=(9.5,9.5,2.1) rot=(0,0,1;0rad)
  Width = 21
FEATURE [Part::Box] Box148  label="Cube132"
  AttacherType = Attacher::AttachEngine3D
  Height = 14
  Length = 17
  Placement = pos=(11.5,11.5,0) rot=(0,0,1;0rad)
  Width = 17
FEATURE [Part::Cut] Cut043
  Base = -> Box147
  Tool = -> Box148
FEATURE [Part::Chamfer] Chamfer014
  Base = -> Cut043
  Edges = 8 edges r=0.95: [Edge4,Edge5,Edge14,Edge16,Edge17,Edge18,Edge19,Edge20]
FEATURE [Part::Cut] Cut047
  Base = -> Cut003
  Tool = -> Chamfer007
FEATURE [Part::Cut] Cut048
  Base = -> Cut047
  Tool = -> Chamfer008
FEATURE [Part::Cut] Cut049  label="Centre Block"
  Base = -> Cut048
  Tool = -> Box085
FEATURE [Part::Cylinder] Cylinder024
  Angle = 360
  AttacherType = Attacher::AttachEngine3D
  Height = 10
  Placement = pos=(6,6,-5) rot=(0,0,1;0rad)
  Radius = 1.7
FEATURE [Part::Cylinder] Cylinder025
  Angle = 360
  AttacherType = Attacher::AttachEngine3D
  Height = 10
  Placement = pos=(34,20,-5) rot=(0,0,1;0rad)
  Radius = 1.7
FEATURE [Part::Cylinder] Cylinder026
  Angle = 360
  AttacherType = Attacher::AttachEngine3D
  Height = 10
  Placement = pos=(6,34,-5) rot=(0,0,1;0rad)
  Radius = 1.7
FEATURE [Part::MultiFuse] Fusion052  label="Screw Holes to remove ball mags"
  Shapes = -> [Cylinder024,Cylinder025,Cylinder026]
FEATURE [Drawing::FeatureViewAnnotation] Annotation
  Font = Sans
  Rotation = 0
  Scale = 7
  Text = 0.4Added in Holes to Mag plate for removal of magnet
  ViewResult = <g transform="translate(14,23) rotate(0)">\n<text id="Annotation"\n font-family="Sans"\n font-size="7"\n fill="#000000">\n<tspan x="0" dy="1em">0.4Added in Holes to Mag plate for removal of magnet</tspan>\n</text>\n</g>
  Visible = false
  X = 14
  Y = 23
FEATURE [Part::Box] Box149  label="Re-level Edge Clip Block001"
  AttacherType = Attacher::AttachEngine3D
  Height = 10
  Length = 12
  Placement = pos=(-21.5,-2,-7) rot=(0,0,1;0rad)
  Width = 44
FEATURE [Part::Fuse] Fusion  label="Bumps"
  Base = -> Sphere008
  Tool = -> Sphere009
FEATURE [Part::Fuse] Fusion053  label="Holes"
  Base = -> Sphere010
  Tool = -> Sphere011
FEATURE [Part::MultiFuse] Fusion054
  Shapes = -> [Box001,Box002,Box003,Box004,Box005]
FEATURE [Part::Fuse] Fusion055
  Base = -> Fusion
  Tool = -> Fusion054
FEATURE [Part::Cut] Cut
  Base = -> Fusion055
  Tool = -> Fusion053
FEATURE [Part::Cut] Cut056
  Base = -> Cut
  Tool = -> Fusion003
FEATURE [Part::Cut] Cut057
  Base = -> Cut056
  Tool = -> Box013
FEATURE [Part::Cut] Cut058
  Base = -> Cut057
  Tool = -> Box149
FEATURE [Part::Cut] Cut059  label="Edge Clips Master"
  Base = -> Cut058
  Tool = -> Box006
FEATURE [Part::Box] Box150  label="Cube133"
  AttacherType = Attacher::AttachEngine3D
  Height = 7
  Length = 5
  Placement = pos=(-5,0,-2) rot=(0,0,1;0rad)
  Width = 40
FEATURE [Part::Box] Box151  label="Cube134"
  AttacherType = Attacher::AttachEngine3D
  Height = 7
  Length = 10
  Placement = pos=(-15,6,-2) rot=(0,0,1;0rad)
  Width = 2
FEATURE [Part::Box] Box152  label="Cube135"
  AttacherType = Attacher::AttachEngine3D
  Height = 7
  Length = 10
  Placement = pos=(-15,10,-2) rot=(0,0,1;0rad)
  Width = 2
FEATURE [Part::Box] Box153  label="Cube136"
  AttacherType = Attacher::AttachEngine3D
  Height = 7
  Length = 10
  Placement = pos=(-15,25.4,-2) rot=(0,0,1;0rad)
  Width = 2
FEATURE [Part::Box] Box154  label="Cube137"
  AttacherType = Attacher::AttachEngine3D
  Height = 7
  Length = 10
  Placement = pos=(-15,34.6,-2) rot=(0,0,1;0rad)
  Width = 2
FEATURE [Part::Sphere] Sphere051
  Angle1 = -90
  Angle2 = 90
  Angle3 = 360
  AttacherType = Attacher::AttachEngine3D
  Placement = pos=(-7.5,6.5,0.5) rot=(0,0,1;0rad)
  Radius = 1.25
FEATURE [Part::Box] Box155  label="Chamfer Cube001"
  AttacherType = Attacher::AttachEngine3D
  Height = 10
  Length = 13
  Placement = pos=(-11.69,0,-1.19) rot=(0,-1,0;0.785398rad)
  Width = 40
FEATURE [Part::Sphere] Sphere052
  Angle1 = -90
  Angle2 = 90
  Angle3 = 360
  AttacherType = Attacher::AttachEngine3D
  Placement = pos=(-7.5,11.5,0.5) rot=(0,0,1;0rad)
  Radius = 1.25
FEATURE [Part::Sphere] Sphere053
  Angle1 = -90
  Angle2 = 90
  Angle3 = 360
  AttacherType = Attacher::AttachEngine3D
  Placement = pos=(-7.5,28,0.5) rot=(0,0,1;0rad)
  Radius = 1.5
FEATURE [Part::Sphere] Sphere054
  Angle1 = -90
  Angle2 = 90
  Angle3 = 360
  AttacherType = Attacher::AttachEngine3D
  Placement = pos=(-7.5,34,0.5) rot=(0,0,1;0rad)
  Radius = 1.5
FEATURE [Part::Box] Box156  label="Cube138"
  AttacherType = Attacher::AttachEngine3D
  Height = 7
  Length = 4
  Placement = pos=(-6,5,-2) rot=(0,0,1;0rad)
  Width = 1
FEATURE [Part::Box] Box157  label="Cube139"
  AttacherType = Attacher::AttachEngine3D
  Height = 7
  Length = 4
  Placement = pos=(-6,8,-2) rot=(0,0,1;0rad)
  Width = 2
FEATURE [Part::Box] Box158  label="Cube140"
  AttacherType = Attacher::AttachEngine3D
  Height = 7
  Length = 4
  Placement = pos=(-6,12,-2) rot=(0,0,1;0rad)
  Width = 1
FEATURE [Part::Box] Box159  label="Cube141"
  AttacherType = Attacher::AttachEngine3D
  Height = 7
  Length = 4
  Placement = pos=(-6,24.4,-2) rot=(0,0,1;0rad)
  Width = 1
FEATURE [Part::Box] Box160  label="Cube142"
  AttacherType = Attacher::AttachEngine3D
  Height = 7
  Length = 4
  Placement = pos=(-6,36.6,-2) rot=(0,0,1;0rad)
  Width = 1
FEATURE [Part::Box] Box161  label="Cube143"
  AttacherType = Attacher::AttachEngine3D
  Height = 7
  Length = 4
  Placement = pos=(-6,27.4,-2) rot=(0,0,1;0rad)
  Width = 7.2
FEATURE [Part::MultiFuse] Fusion056  label="Extra Holes for Clips001"
  Shapes = -> [Box161,Box158,Box160,Box157,Box159,Box156]
FEATURE [Part::Box] Box162  label="Re-level Edge Clip Block002"
  AttacherType = Attacher::AttachEngine3D
  Height = 10
  Length = 20
  Placement = pos=(-19,-2,3) rot=(0,0,1;0rad)
  Width = 44
FEATURE [Part::Box] Box163  label="Re-level Edge Clip Block003"
  AttacherType = Attacher::AttachEngine3D
  Height = 10
  Length = 12
  Placement = pos=(-21.5,-2,-7) rot=(0,0,1;0rad)
  Width = 44
FEATURE [Part::Fuse] Fusion057  label="Bumps001"
  Base = -> Sphere051
  Tool = -> Sphere052
FEATURE [Part::Fuse] Fusion058  label="Holes001"
  Base = -> Sphere053
  Tool = -> Sphere054
FEATURE [Part::MultiFuse] Fusion059
  Shapes = -> [Box150,Box151,Box152,Box153,Box154]
FEATURE [Part::Fuse] Fusion060
  Base = -> Fusion057
  Tool = -> Fusion059
FEATURE [Part::Cut] Cut060
  Base = -> Fusion060
  Tool = -> Fusion058
FEATURE [Part::Cut] Cut061
  Base = -> Cut060
  Tool = -> Fusion056
FEATURE [Part::Cut] Cut062
  Base = -> Cut061
  Tool = -> Box162
FEATURE [Part::Cut] Cut063
  Base = -> Cut062
  Tool = -> Box163
FEATURE [Part::Cut] Cut064  label="Copy Edge Clips"
  Base = -> Cut063
  Placement = pos=(-7,40,-7) rot=(0.707107,0,-0.707107;3.14159rad)
  Tool = -> Box155
FEATURE [App::DocumentObjectGroup] Group001  label="Old"
  Group = -> [Cut008,Cut009,Cut015,Cut018,Fusion021,Fusion023,Group,Cut039,Cut028,Cut032,Cut033,Fusion048]
FEATURE [Part::Box] Box164  label="Cube144"
  AttacherType = Attacher::AttachEngine3D
  Height = 7
  Length = 5
  Placement = pos=(-5,0,-2) rot=(0,0,1;0rad)
  Width = 40
FEATURE [Part::Box] Box165  label="Cube145"
  AttacherType = Attacher::AttachEngine3D
  Height = 7
  Length = 10
  Placement = pos=(-15,6,-2) rot=(0,0,1;0rad)
  Width = 2
FEATURE [Part::Box] Box166  label="Cube146"
  AttacherType = Attacher::AttachEngine3D
  Height = 7
  Length = 10
  Placement = pos=(-15,10,-2) rot=(0,0,1;0rad)
  Width = 2
FEATURE [Part::Box] Box167  label="Cube147"
  AttacherType = Attacher::AttachEngine3D
  Height = 7
  Length = 10
  Placement = pos=(-15,25.4,-2) rot=(0,0,1;0rad)
  Width = 2
FEATURE [Part::Box] Box168  label="Cube148"
  AttacherType = Attacher::AttachEngine3D
  Height = 7
  Length = 10
  Placement = pos=(-15,34.6,-2) rot=(0,0,1;0rad)
  Width = 2
FEATURE [Part::Sphere] Sphere055
  Angle1 = -90
  Angle2 = 90
  Angle3 = 360
  AttacherType = Attacher::AttachEngine3D
  Placement = pos=(-7.5,6.5,0.5) rot=(0,0,1;0rad)
  Radius = 1.25
FEATURE [Part::Box] Box169  label="Chamfer Cube002"
  AttacherType = Attacher::AttachEngine3D
  Height = 10
  Length = 13
  Placement = pos=(-11.69,0,-1.19) rot=(0,-1,0;0.785398rad)
  Width = 40
FEATURE [Part::Sphere] Sphere056
  Angle1 = -90
  Angle2 = 90
  Angle3 = 360
  AttacherType = Attacher::AttachEngine3D
  Placement = pos=(-7.5,11.5,0.5) rot=(0,0,1;0rad)
  Radius = 1.25
FEATURE [Part::Sphere] Sphere057
  Angle1 = -90
  Angle2 = 90
  Angle3 = 360
  AttacherType = Attacher::AttachEngine3D
  Placement = pos=(-7.5,28,0.5) rot=(0,0,1;0rad)
  Radius = 1.5
FEATURE [Part::Sphere] Sphere058
  Angle1 = -90
  Angle2 = 90
  Angle3 = 360
  AttacherType = Attacher::AttachEngine3D
  Placement = pos=(-7.5,34,0.5) rot=(0,0,1;0rad)
  Radius = 1.5
FEATURE [Part::Box] Box170  label="Cube149"
  AttacherType = Attacher::AttachEngine3D
  Height = 7
  Length = 4
  Placement = pos=(-6,5,-2) rot=(0,0,1;0rad)
  Width = 1
FEATURE [Part::Box] Box171  label="Cube150"
  AttacherType = Attacher::AttachEngine3D
  Height = 7
  Length = 4
  Placement = pos=(-6,8,-2) rot=(0,0,1;0rad)
  Width = 2
FEATURE [Part::Box] Box172  label="Cube151"
  AttacherType = Attacher::AttachEngine3D
  Height = 7
  Length = 4
  Placement = pos=(-6,12,-2) rot=(0,0,1;0rad)
  Width = 1
FEATURE [Part::Box] Box173  label="Cube152"
  AttacherType = Attacher::AttachEngine3D
  Height = 7
  Length = 4
  Placement = pos=(-6,24.4,-2) rot=(0,0,1;0rad)
  Width = 1
FEATURE [Part::Box] Box174  label="Cube153"
  AttacherType = Attacher::AttachEngine3D
  Height = 7
  Length = 4
  Placement = pos=(-6,36.6,-2) rot=(0,0,1;0rad)
  Width = 1
FEATURE [Part::Box] Box175  label="Cube154"
  AttacherType = Attacher::AttachEngine3D
  Height = 7
  Length = 4
  Placement = pos=(-6,27.4,-2) rot=(0,0,1;0rad)
  Width = 7.2
FEATURE [Part::MultiFuse] Fusion061  label="Extra Holes for Clips002"
  Shapes = -> [Box175,Box172,Box174,Box171,Box173,Box170]
FEATURE [Part::Box] Box176  label="Re-level Edge Clip Block004"
  AttacherType = Attacher::AttachEngine3D
  Height = 10
  Length = 20
  Placement = pos=(-19,-2,3) rot=(0,0,1;0rad)
  Width = 44
FEATURE [Part::Box] Box177  label="Re-level Edge Clip Block005"
  AttacherType = Attacher::AttachEngine3D
  Height = 10
  Length = 12
  Placement = pos=(-21.5,-2,-7) rot=(0,0,1;0rad)
  Width = 44
FEATURE [Part::Fuse] Fusion062  label="Bumps002"
  Base = -> Sphere055
  Tool = -> Sphere056
FEATURE [Part::Fuse] Fusion063  label="Holes002"
  Base = -> Sphere057
  Tool = -> Sphere058
FEATURE [Part::MultiFuse] Fusion064
  Shapes = -> [Box164,Box165,Box166,Box167,Box168]
FEATURE [Part::Fuse] Fusion065
  Base = -> Fusion062
  Tool = -> Fusion064
FEATURE [Part::Cut] Cut065
  Base = -> Fusion065
  Tool = -> Fusion063
FEATURE [Part::Cut] Cut066
  Base = -> Cut065
  Tool = -> Fusion061
FEATURE [Part::Cut] Cut067
  Base = -> Cut066
  Tool = -> Box176
FEATURE [Part::Cut] Cut068
  Base = -> Cut067
  Tool = -> Box177
FEATURE [Part::Cut] Cut069  label="Edge Clips001"
  Base = -> Cut068
  Placement = pos=(40,0,0) rot=(0,0,1;1.5708rad)
  Tool = -> Box169
FEATURE [Part::Box] Box178  label="Cube155"
  AttacherType = Attacher::AttachEngine3D
  Height = 7
  Length = 5
  Placement = pos=(-5,0,-2) rot=(0,0,1;0rad)
  Width = 40
FEATURE [Part::Box] Box179  label="Cube156"
  AttacherType = Attacher::AttachEngine3D
  Height = 7
  Length = 10
  Placement = pos=(-15,10,-2) rot=(0,0,1;0rad)
  Width = 2
FEATURE [Part::Box] Box180  label="Re-level Edge Clip Block006"
  AttacherType = Attacher::AttachEngine3D
  Height = 10
  Length = 20
  Placement = pos=(-19,-2,3) rot=(0,0,1;0rad)
  Width = 44
FEATURE [Part::Box] Box181  label="Cube157"
  AttacherType = Attacher::AttachEngine3D
  Height = 7
  Length = 4
  Placement = pos=(-6,27.4,-2) rot=(0,0,1;0rad)
  Width = 7.2
FEATURE [Part::Box] Box182  label="Cube158"
  AttacherType = Attacher::AttachEngine3D
  Height = 7
  Length = 4
  Placement = pos=(-6,12,-2) rot=(0,0,1;0rad)
  Width = 1
FEATURE [Part::Sphere] Sphere059
  Angle1 = -90
  Angle2 = 90
  Angle3 = 360
  AttacherType = Attacher::AttachEngine3D
  Placement = pos=(-7.5,6.5,0.5) rot=(0,0,1;0rad)
  Radius = 1.25
FEATURE [Part::Box] Box183  label="Cube159"
  AttacherType = Attacher::AttachEngine3D
  Height = 7
  Length = 10
  Placement = pos=(-15,25.4,-2) rot=(0,0,1;0rad)
  Width = 2
FEATURE [Part::Box] Box184  label="Cube160"
  AttacherType = Attacher::AttachEngine3D
  Height = 7
  Length = 4
  Placement = pos=(-6,36.6,-2) rot=(0,0,1;0rad)
  Width = 1
FEATURE [Part::Sphere] Sphere060
  Angle1 = -90
  Angle2 = 90
  Angle3 = 360
  AttacherType = Attacher::AttachEngine3D
  Placement = pos=(-7.5,34,0.5) rot=(0,0,1;0rad)
  Radius = 1.5
FEATURE [Part::Box] Box185  label="Cube161"
  AttacherType = Attacher::AttachEngine3D
  Height = 7
  Length = 4
  Placement = pos=(-6,24.4,-2) rot=(0,0,1;0rad)
  Width = 1
FEATURE [Part::Box] Box186  label="Cube162"
  AttacherType = Attacher::AttachEngine3D
  Height = 7
  Length = 4
  Placement = pos=(-6,8,-2) rot=(0,0,1;0rad)
  Width = 2
FEATURE [Part::Box] Box187  label="Re-level Edge Clip Block007"
  AttacherType = Attacher::AttachEngine3D
  Height = 10
  Length = 12
  Placement = pos=(-21.5,-2,-7) rot=(0,0,1;0rad)
  Width = 44
FEATURE [Part::Sphere] Sphere061
  Angle1 = -90
  Angle2 = 90
  Angle3 = 360
  AttacherType = Attacher::AttachEngine3D
  Placement = pos=(-7.5,11.5,0.5) rot=(0,0,1;0rad)
  Radius = 1.25
FEATURE [Part::Sphere] Sphere062
  Angle1 = -90
  Angle2 = 90
  Angle3 = 360
  AttacherType = Attacher::AttachEngine3D
  Placement = pos=(-7.5,28,0.5) rot=(0,0,1;0rad)
  Radius = 1.5
FEATURE [Part::Fuse] Fusion066  label="Holes003"
  Base = -> Sphere062
  Tool = -> Sphere060
FEATURE [Part::Box] Box188  label="Cube163"
  AttacherType = Attacher::AttachEngine3D
  Height = 7
  Length = 10
  Placement = pos=(-15,34.6,-2) rot=(0,0,1;0rad)
  Width = 2
FEATURE [Part::Box] Box189  label="Cube164"
  AttacherType = Attacher::AttachEngine3D
  Height = 7
  Length = 4
  Placement = pos=(-6,5,-2) rot=(0,0,1;0rad)
  Width = 1
FEATURE [Part::MultiFuse] Fusion067  label="Extra Holes for Clips003"
  Shapes = -> [Box181,Box182,Box184,Box186,Box185,Box189]
FEATURE [Part::Box] Box190  label="Cube165"
  AttacherType = Attacher::AttachEngine3D
  Height = 7
  Length = 10
  Placement = pos=(-15,6,-2) rot=(0,0,1;0rad)
  Width = 2
FEATURE [Part::MultiFuse] Fusion069
  Shapes = -> [Box178,Box190,Box179,Box183,Box188]
FEATURE [Part::Fuse] Fusion070  label="Bumps003"
  Base = -> Sphere059
  Tool = -> Sphere061
FEATURE [Part::Fuse] Fusion068
  Base = -> Fusion070
  Tool = -> Fusion069
FEATURE [Part::Cut] Cut073
  Base = -> Fusion068
  Tool = -> Fusion066
FEATURE [Part::Cut] Cut070
  Base = -> Cut073
  Tool = -> Fusion067
FEATURE [Part::Cut] Cut071
  Base = -> Cut070
  Tool = -> Box180
FEATURE [Part::Cut] Cut072
  Base = -> Cut071
  Tool = -> Box187
FEATURE [Part::Box] Box191  label="Chamfer Cube003"
  AttacherType = Attacher::AttachEngine3D
  Height = 10
  Length = 13
  Placement = pos=(-11.69,0,-1.19) rot=(0,-1,0;0.785398rad)
  Width = 40
FEATURE [Part::Cut] Cut074  label="Edge Clips002"
  Base = -> Cut072
  Placement = pos=(40,40,0) rot=(0,0,1;3.14159rad)
  Tool = -> Box191
FEATURE [Part::Box] Box192  label="Cube166"
  AttacherType = Attacher::AttachEngine3D
  Height = 7
  Length = 10
  Placement = pos=(-15,6,-2) rot=(0,0,1;0rad)
  Width = 2
FEATURE [Part::Box] Box193  label="Chamfer Cube004"
  AttacherType = Attacher::AttachEngine3D
  Height = 10
  Length = 13
  Placement = pos=(-11.69,0,-1.19) rot=(0,-1,0;0.785398rad)
  Width = 40
FEATURE [Part::Box] Box194  label="Re-level Edge Clip Block008"
  AttacherType = Attacher::AttachEngine3D
  Height = 10
  Length = 20
  Placement = pos=(-19,-2,3) rot=(0,0,1;0rad)
  Width = 44
FEATURE [Part::Box] Box195  label="Cube167"
  AttacherType = Attacher::AttachEngine3D
  Height = 7
  Length = 10
  Placement = pos=(-15,10,-2) rot=(0,0,1;0rad)
  Width = 2
FEATURE [Part::Box] Box196  label="Cube168"
  AttacherType = Attacher::AttachEngine3D
  Height = 7
  Length = 5
  Placement = pos=(-5,0,-2) rot=(0,0,1;0rad)
  Width = 40
FEATURE [Part::Box] Box197  label="Cube169"
  AttacherType = Attacher::AttachEngine3D
  Height = 7
  Length = 4
  Placement = pos=(-6,5,-2) rot=(0,0,1;0rad)
  Width = 1
FEATURE [Part::Box] Box198  label="Cube170"
  AttacherType = Attacher::AttachEngine3D
  Height = 7
  Length = 4
  Placement = pos=(-6,12,-2) rot=(0,0,1;0rad)
  Width = 1
FEATURE [Part::Box] Box199  label="Cube171"
  AttacherType = Attacher::AttachEngine3D
  Height = 7
  Length = 4
  Placement = pos=(-6,27.4,-2) rot=(0,0,1;0rad)
  Width = 7.2
FEATURE [Part::Box] Box200  label="Cube172"
  AttacherType = Attacher::AttachEngine3D
  Height = 7
  Length = 4
  Placement = pos=(-6,24.4,-2) rot=(0,0,1;0rad)
  Width = 1
FEATURE [Part::Sphere] Sphere063
  Angle1 = -90
  Angle2 = 90
  Angle3 = 360
  AttacherType = Attacher::AttachEngine3D
  Placement = pos=(-7.5,28,0.5) rot=(0,0,1;0rad)
  Radius = 1.5
FEATURE [Part::Sphere] Sphere064
  Angle1 = -90
  Angle2 = 90
  Angle3 = 360
  AttacherType = Attacher::AttachEngine3D
  Placement = pos=(-7.5,11.5,0.5) rot=(0,0,1;0rad)
  Radius = 1.25
FEATURE [Part::Box] Box201  label="Cube173"
  AttacherType = Attacher::AttachEngine3D
  Height = 7
  Length = 4
  Placement = pos=(-6,8,-2) rot=(0,0,1;0rad)
  Width = 2
FEATURE [Part::Box] Box202  label="Cube174"
  AttacherType = Attacher::AttachEngine3D
  Height = 7
  Length = 10
  Placement = pos=(-15,25.4,-2) rot=(0,0,1;0rad)
  Width = 2
FEATURE [Part::Sphere] Sphere065
  Angle1 = -90
  Angle2 = 90
  Angle3 = 360
  AttacherType = Attacher::AttachEngine3D
  Placement = pos=(-7.5,6.5,0.5) rot=(0,0,1;0rad)
  Radius = 1.25
FEATURE [Part::Fuse] Fusion073  label="Bumps004"
  Base = -> Sphere065
  Tool = -> Sphere064
FEATURE [Part::Sphere] Sphere066
  Angle1 = -90
  Angle2 = 90
  Angle3 = 360
  AttacherType = Attacher::AttachEngine3D
  Placement = pos=(-7.5,34,0.5) rot=(0,0,1;0rad)
  Radius = 1.5
FEATURE [Part::Fuse] Fusion071  label="Holes004"
  Base = -> Sphere063
  Tool = -> Sphere066
FEATURE [Part::Box] Box203  label="Re-level Edge Clip Block009"
  AttacherType = Attacher::AttachEngine3D
  Height = 10
  Length = 12
  Placement = pos=(-21.5,-2,-7) rot=(0,0,1;0rad)
  Width = 44
FEATURE [Part::Box] Box204  label="Cube175"
  AttacherType = Attacher::AttachEngine3D
  Height = 7
  Length = 4
  Placement = pos=(-6,36.6,-2) rot=(0,0,1;0rad)
  Width = 1
FEATURE [Part::MultiFuse] Fusion074  label="Extra Holes for Clips004"
  Shapes = -> [Box199,Box198,Box204,Box201,Box200,Box197]
FEATURE [Part::Box] Box205  label="Cube176"
  AttacherType = Attacher::AttachEngine3D
  Height = 7
  Length = 10
  Placement = pos=(-15,34.6,-2) rot=(0,0,1;0rad)
  Width = 2
FEATURE [Part::MultiFuse] Fusion072
  Shapes = -> [Box196,Box192,Box195,Box202,Box205]
FEATURE [Part::Fuse] Fusion075
  Base = -> Fusion073
  Tool = -> Fusion072
FEATURE [Part::Cut] Cut075
  Base = -> Fusion075
  Tool = -> Fusion071
FEATURE [Part::Cut] Cut076
  Base = -> Cut075
  Tool = -> Fusion074
FEATURE [Part::Cut] Cut078
  Base = -> Cut076
  Tool = -> Box194
FEATURE [Part::Cut] Cut077
  Base = -> Cut078
  Tool = -> Box203
FEATURE [Part::Cut] Cut079  label="Edge Clips003"
  Base = -> Cut077
  Placement = pos=(0,40,0) rot=(0,0,-1;1.5708rad)
  Tool = -> Box193
FEATURE [Part::MultiFuse] Fusion076  label="Edge Clips Fusion"
  Shapes = -> [Cut059,Cut069,Cut074,Cut079]
FEATURE [Part::Cut] Cut080
  Base = -> Cut049
  Tool = -> Fusion052
FEATURE [Part::Fuse] Fusion077
  Base = -> Fusion076
  Tool = -> Cut080
FEATURE [Part::Box] Box206  label="Cube177"
  AttacherType = Attacher::AttachEngine3D
  Height = 10
  Length = 10
  Placement = pos=(46,24,1) rot=(0.442189,-0.287968,0.849437;1.66134rad)
  Width = 15
FEATURE [Part::Box] Box207  label="Cube178"
  AttacherType = Attacher::AttachEngine3D
  Height = 10
  Length = 10
  Placement = pos=(16,46,1) rot=(0.381439,0.080566,0.920876;3.07487rad)
  Width = 15
FEATURE [Part::Box] Box208  label="Cube179"
  AttacherType = Attacher::AttachEngine3D
  Height = 10
  Length = 10
  Placement = pos=(-6,16,1) rot=(-0.273007,-0.419215,-0.865867;1.78566rad)
  Width = 15
FEATURE [Part::MultiFuse] Fusion078  label="Glue Dents"
  Shapes = -> [Box086,Box208,Box207,Box206]
FEATURE [Part::Cut] Cut081  label="Ball Plate"
  Base = -> Fusion077
  Tool = -> Fusion078
FEATURE [Part::Box] Box209  label="Cube180"
  AttacherType = Attacher::AttachEngine3D
  Height = 7
  Length = 5
  Placement = pos=(-5,0,-2) rot=(0,0,1;0rad)
  Width = 40
FEATURE [Part::Box] Box210  label="Cube181"
  AttacherType = Attacher::AttachEngine3D
  Height = 7
  Length = 10
  Placement = pos=(-15,6,-2) rot=(0,0,1;0rad)
  Width = 2
FEATURE [Part::Box] Box211  label="Cube182"
  AttacherType = Attacher::AttachEngine3D
  Height = 7
  Length = 10
  Placement = pos=(-15,10,-2) rot=(0,0,1;0rad)
  Width = 2
FEATURE [Part::Box] Box212  label="Cube183"
  AttacherType = Attacher::AttachEngine3D
  Height = 7
  Length = 10
  Placement = pos=(-15,25.4,-2) rot=(0,0,1;0rad)
  Width = 2
FEATURE [Part::Box] Box213  label="Cube184"
  AttacherType = Attacher::AttachEngine3D
  Height = 7
  Length = 10
  Placement = pos=(-15,34.6,-2) rot=(0,0,1;0rad)
  Width = 2
FEATURE [Part::Sphere] Sphere067
  Angle1 = -90
  Angle2 = 90
  Angle3 = 360
  AttacherType = Attacher::AttachEngine3D
  Placement = pos=(-7.5,6.5,0.5) rot=(0,0,1;0rad)
  Radius = 1.25
FEATURE [Part::Box] Box214  label="Chamfer Cube005"
  AttacherType = Attacher::AttachEngine3D
  Height = 10
  Length = 13
  Placement = pos=(-11.69,0,-1.19) rot=(0,-1,0;0.785398rad)
  Width = 40
FEATURE [Part::Sphere] Sphere068
  Angle1 = -90
  Angle2 = 90
  Angle3 = 360
  AttacherType = Attacher::AttachEngine3D
  Placement = pos=(-7.5,11.5,0.5) rot=(0,0,1;0rad)
  Radius = 1.25
FEATURE [Part::Sphere] Sphere069
  Angle1 = -90
  Angle2 = 90
  Angle3 = 360
  AttacherType = Attacher::AttachEngine3D
  Placement = pos=(-7.5,28,0.5) rot=(0,0,1;0rad)
  Radius = 1.5
FEATURE [Part::Sphere] Sphere070
  Angle1 = -90
  Angle2 = 90
  Angle3 = 360
  AttacherType = Attacher::AttachEngine3D
  Placement = pos=(-7.5,34,0.5) rot=(0,0,1;0rad)
  Radius = 1.5
FEATURE [Part::Box] Box215  label="Cube185"
  AttacherType = Attacher::AttachEngine3D
  Height = 7
  Length = 4
  Placement = pos=(-6,5,-2) rot=(0,0,1;0rad)
  Width = 1
FEATURE [Part::Box] Box216  label="Cube186"
  AttacherType = Attacher::AttachEngine3D
  Height = 7
  Length = 4
  Placement = pos=(-6,8,-2) rot=(0,0,1;0rad)
  Width = 2
FEATURE [Part::Box] Box217  label="Cube187"
  AttacherType = Attacher::AttachEngine3D
  Height = 7
  Length = 4
  Placement = pos=(-6,12,-2) rot=(0,0,1;0rad)
  Width = 1
FEATURE [Part::Box] Box218  label="Cube188"
  AttacherType = Attacher::AttachEngine3D
  Height = 7
  Length = 4
  Placement = pos=(-6,24.4,-2) rot=(0,0,1;0rad)
  Width = 1
FEATURE [Part::Box] Box219  label="Cube189"
  AttacherType = Attacher::AttachEngine3D
  Height = 7
  Length = 4
  Placement = pos=(-6,36.6,-2) rot=(0,0,1;0rad)
  Width = 1
FEATURE [Part::Box] Box220  label="Cube190"
  AttacherType = Attacher::AttachEngine3D
  Height = 7
  Length = 4
  Placement = pos=(-6,27.4,-2) rot=(0,0,1;0rad)
  Width = 7.2
FEATURE [Part::MultiFuse] Fusion079  label="Extra Holes for Clips005"
  Shapes = -> [Box220,Box217,Box219,Box216,Box218,Box215]
FEATURE [Part::Box] Box221  label="Re-level Edge Clip Block010"
  AttacherType = Attacher::AttachEngine3D
  Height = 10
  Length = 20
  Placement = pos=(-19,-2,3) rot=(0,0,1;0rad)
  Width = 44
FEATURE [Part::Box] Box222  label="Re-level Edge Clip Block011"
  AttacherType = Attacher::AttachEngine3D
  Height = 10
  Length = 12
  Placement = pos=(-21.5,-2,-7) rot=(0,0,1;0rad)
  Width = 44
FEATURE [Part::Fuse] Fusion080  label="Bumps005"
  Base = -> Sphere067
  Tool = -> Sphere068
FEATURE [Part::Fuse] Fusion081  label="Holes005"
  Base = -> Sphere069
  Tool = -> Sphere070
FEATURE [Part::MultiFuse] Fusion082
  Shapes = -> [Box209,Box210,Box211,Box212,Box213]
FEATURE [Part::Fuse] Fusion083
  Base = -> Fusion080
  Tool = -> Fusion082
FEATURE [Part::Cut] Cut082
  Base = -> Fusion083
  Tool = -> Fusion081
FEATURE [Part::Cut] Cut083
  Base = -> Cut082
  Tool = -> Fusion079
FEATURE [Part::Cut] Cut084
  Base = -> Cut083
  Tool = -> Box221
FEATURE [Part::Cut] Cut085
  Base = -> Cut084
  Tool = -> Box222
FEATURE [Part::Cut] Cut086  label="Edge Clips Master001"
  Base = -> Cut085
  Tool = -> Box214
FEATURE [Part::Box] Box223  label="Cube191"
  AttacherType = Attacher::AttachEngine3D
  Height = 7
  Length = 5
  Placement = pos=(-5,0,-2) rot=(0,0,1;0rad)
  Width = 40
FEATURE [Part::Box] Box224  label="Cube192"
  AttacherType = Attacher::AttachEngine3D
  Height = 7
  Length = 4
  Placement = pos=(-6,8,-2) rot=(0,0,1;0rad)
  Width = 2
FEATURE [Part::Box] Box225  label="Chamfer Cube006"
  AttacherType = Attacher::AttachEngine3D
  Height = 10
  Length = 13
  Placement = pos=(-11.69,0,-1.19) rot=(0,-1,0;0.785398rad)
  Width = 40
FEATURE [Part::Box] Box226  label="Cube193"
  AttacherType = Attacher::AttachEngine3D
  Height = 7
  Length = 10
  Placement = pos=(-15,6,-2) rot=(0,0,1;0rad)
  Width = 2
FEATURE [Part::Sphere] Sphere071
  Angle1 = -90
  Angle2 = 90
  Angle3 = 360
  AttacherType = Attacher::AttachEngine3D
  Placement = pos=(-7.5,11.5,0.5) rot=(0,0,1;0rad)
  Radius = 1.25
FEATURE [Part::Box] Box227  label="Cube194"
  AttacherType = Attacher::AttachEngine3D
  Height = 7
  Length = 4
  Placement = pos=(-6,27.4,-2) rot=(0,0,1;0rad)
  Width = 7.2
FEATURE [Part::Box] Box228  label="Cube195"
  AttacherType = Attacher::AttachEngine3D
  Height = 7
  Length = 4
  Placement = pos=(-6,12,-2) rot=(0,0,1;0rad)
  Width = 1
FEATURE [Part::Box] Box229  label="Cube196"
  AttacherType = Attacher::AttachEngine3D
  Height = 7
  Length = 4
  Placement = pos=(-6,24.4,-2) rot=(0,0,1;0rad)
  Width = 1
FEATURE [Part::Sphere] Sphere072
  Angle1 = -90
  Angle2 = 90
  Angle3 = 360
  AttacherType = Attacher::AttachEngine3D
  Placement = pos=(-7.5,6.5,0.5) rot=(0,0,1;0rad)
  Radius = 1.25
FEATURE [Part::Box] Box230  label="Cube197"
  AttacherType = Attacher::AttachEngine3D
  Height = 7
  Length = 4
  Placement = pos=(-6,36.6,-2) rot=(0,0,1;0rad)
  Width = 1
FEATURE [Part::Box] Box231  label="Cube198"
  AttacherType = Attacher::AttachEngine3D
  Height = 7
  Length = 10
  Placement = pos=(-15,10,-2) rot=(0,0,1;0rad)
  Width = 2
FEATURE [Part::Sphere] Sphere073
  Angle1 = -90
  Angle2 = 90
  Angle3 = 360
  AttacherType = Attacher::AttachEngine3D
  Placement = pos=(-7.5,34,0.5) rot=(0,0,1;0rad)
  Radius = 1.5
FEATURE [Part::Box] Box232  label="Cube199"
  AttacherType = Attacher::AttachEngine3D
  Height = 7
  Length = 4
  Placement = pos=(-6,5,-2) rot=(0,0,1;0rad)
  Width = 1
FEATURE [Part::MultiFuse] Fusion085  label="Extra Holes for Clips006"
  Shapes = -> [Box227,Box228,Box230,Box224,Box229,Box232]
FEATURE [Part::Box] Box233  label="Re-level Edge Clip Block012"
  AttacherType = Attacher::AttachEngine3D
  Height = 10
  Length = 20
  Placement = pos=(-19,-2,3) rot=(0,0,1;0rad)
  Width = 44
FEATURE [Part::Box] Box234  label="Cube200"
  AttacherType = Attacher::AttachEngine3D
  Height = 7
  Length = 10
  Placement = pos=(-15,34.6,-2) rot=(0,0,1;0rad)
  Width = 2
FEATURE [Part::Box] Box235  label="Cube201"
  AttacherType = Attacher::AttachEngine3D
  Height = 7
  Length = 10
  Placement = pos=(-15,25.4,-2) rot=(0,0,1;0rad)
  Width = 2
FEATURE [Part::MultiFuse] Fusion086
  Shapes = -> [Box223,Box226,Box231,Box235,Box234]
FEATURE [Part::Fuse] Fusion087  label="Bumps006"
  Base = -> Sphere072
  Tool = -> Sphere071
FEATURE [Part::Fuse] Fusion084
  Base = -> Fusion087
  Tool = -> Fusion086
FEATURE [Part::Sphere] Sphere074
  Angle1 = -90
  Angle2 = 90
  Angle3 = 360
  AttacherType = Attacher::AttachEngine3D
  Placement = pos=(-7.5,28,0.5) rot=(0,0,1;0rad)
  Radius = 1.5
FEATURE [Part::Fuse] Fusion088  label="Holes006"
  Base = -> Sphere074
  Tool = -> Sphere073
FEATURE [Part::Box] Box236  label="Re-level Edge Clip Block013"
  AttacherType = Attacher::AttachEngine3D
  Height = 10
  Length = 12
  Placement = pos=(-21.5,-2,-7) rot=(0,0,1;0rad)
  Width = 44
FEATURE [Part::Cut] Cut087
  Base = -> Fusion084
  Tool = -> Fusion088
FEATURE [Part::Cut] Cut088
  Base = -> Cut087
  Tool = -> Fusion085
FEATURE [Part::Cut] Cut089
  Base = -> Cut088
  Tool = -> Box233
FEATURE [Part::Cut] Cut090
  Base = -> Cut089
  Tool = -> Box236
FEATURE [Part::Cut] Cut091  label="Edge Clips004"
  Base = -> Cut090
  Placement = pos=(40,0,0) rot=(0,0,1;1.5708rad)
  Tool = -> Box225
FEATURE [Part::Box] Box237  label="Re-level Edge Clip Block014"
  AttacherType = Attacher::AttachEngine3D
  Height = 10
  Length = 12
  Placement = pos=(-21.5,-2,-7) rot=(0,0,1;0rad)
  Width = 44
FEATURE [Part::Box] Box238  label="Cube202"
  AttacherType = Attacher::AttachEngine3D
  Height = 7
  Length = 4
  Placement = pos=(-6,36.6,-2) rot=(0,0,1;0rad)
  Width = 1
FEATURE [Part::Box] Box239  label="Cube203"
  AttacherType = Attacher::AttachEngine3D
  Height = 7
  Length = 10
  Placement = pos=(-15,10,-2) rot=(0,0,1;0rad)
  Width = 2
FEATURE [Part::Box] Box240  label="Cube204"
  AttacherType = Attacher::AttachEngine3D
  Height = 7
  Length = 10
  Placement = pos=(-15,25.4,-2) rot=(0,0,1;0rad)
  Width = 2
FEATURE [Part::Box] Box241  label="Re-level Edge Clip Block015"
  AttacherType = Attacher::AttachEngine3D
  Height = 10
  Length = 20
  Placement = pos=(-19,-2,3) rot=(0,0,1;0rad)
  Width = 44
FEATURE [Part::Box] Box242  label="Cube205"
  AttacherType = Attacher::AttachEngine3D
  Height = 7
  Length = 10
  Placement = pos=(-15,34.6,-2) rot=(0,0,1;0rad)
  Width = 2
FEATURE [Part::Sphere] Sphere075
  Angle1 = -90
  Angle2 = 90
  Angle3 = 360
  AttacherType = Attacher::AttachEngine3D
  Placement = pos=(-7.5,34,0.5) rot=(0,0,1;0rad)
  Radius = 1.5
FEATURE [Part::Sphere] Sphere076
  Angle1 = -90
  Angle2 = 90
  Angle3 = 360
  AttacherType = Attacher::AttachEngine3D
  Placement = pos=(-7.5,28,0.5) rot=(0,0,1;0rad)
  Radius = 1.5
FEATURE [Part::Fuse] Fusion089  label="Holes007"
  Base = -> Sphere076
  Tool = -> Sphere075
FEATURE [Part::Box] Box243  label="Cube206"
  AttacherType = Attacher::AttachEngine3D
  Height = 7
  Length = 4
  Placement = pos=(-6,5,-2) rot=(0,0,1;0rad)
  Width = 1
FEATURE [Part::Box] Box244  label="Cube207"
  AttacherType = Attacher::AttachEngine3D
  Height = 7
  Length = 4
  Placement = pos=(-6,24.4,-2) rot=(0,0,1;0rad)
  Width = 1
FEATURE [Part::Sphere] Sphere077
  Angle1 = -90
  Angle2 = 90
  Angle3 = 360
  AttacherType = Attacher::AttachEngine3D
  Placement = pos=(-7.5,11.5,0.5) rot=(0,0,1;0rad)
  Radius = 1.25
FEATURE [Part::Box] Box245  label="Cube208"
  AttacherType = Attacher::AttachEngine3D
  Height = 7
  Length = 4
  Placement = pos=(-6,12,-2) rot=(0,0,1;0rad)
  Width = 1
FEATURE [Part::Box] Box246  label="Chamfer Cube007"
  AttacherType = Attacher::AttachEngine3D
  Height = 10
  Length = 13
  Placement = pos=(-11.69,0,-1.19) rot=(0,-1,0;0.785398rad)
  Width = 40
FEATURE [Part::Sphere] Sphere078
  Angle1 = -90
  Angle2 = 90
  Angle3 = 360
  AttacherType = Attacher::AttachEngine3D
  Placement = pos=(-7.5,6.5,0.5) rot=(0,0,1;0rad)
  Radius = 1.25
FEATURE [Part::Fuse] Fusion090  label="Bumps007"
  Base = -> Sphere078
  Tool = -> Sphere077
FEATURE [Part::Box] Box247  label="Cube209"
  AttacherType = Attacher::AttachEngine3D
  Height = 7
  Length = 5
  Placement = pos=(-5,0,-2) rot=(0,0,1;0rad)
  Width = 40
FEATURE [Part::Box] Box248  label="Cube210"
  AttacherType = Attacher::AttachEngine3D
  Height = 7
  Length = 4
  Placement = pos=(-6,27.4,-2) rot=(0,0,1;0rad)
  Width = 7.2
FEATURE [Part::Box] Box249  label="Cube211"
  AttacherType = Attacher::AttachEngine3D
  Height = 7
  Length = 4
  Placement = pos=(-6,8,-2) rot=(0,0,1;0rad)
  Width = 2
FEATURE [Part::MultiFuse] Fusion091  label="Extra Holes for Clips007"
  Shapes = -> [Box248,Box245,Box238,Box249,Box244,Box243]
FEATURE [Part::Box] Box250  label="Cube212"
  AttacherType = Attacher::AttachEngine3D
  Height = 7
  Length = 10
  Placement = pos=(-15,6,-2) rot=(0,0,1;0rad)
  Width = 2
FEATURE [Part::MultiFuse] Fusion092
  Shapes = -> [Box247,Box250,Box239,Box240,Box242]
FEATURE [Part::Fuse] Fusion093
  Base = -> Fusion090
  Tool = -> Fusion092
FEATURE [Part::Cut] Cut093
  Base = -> Fusion093
  Tool = -> Fusion089
FEATURE [Part::Cut] Cut094
  Base = -> Cut093
  Tool = -> Fusion091
FEATURE [Part::Cut] Cut095
  Base = -> Cut094
  Tool = -> Box241
FEATURE [Part::Cut] Cut096
  Base = -> Cut095
  Tool = -> Box237
FEATURE [Part::Cut] Cut092  label="Edge Clips005"
  Base = -> Cut096
  Placement = pos=(40,40,0) rot=(0,0,1;3.14159rad)
  Tool = -> Box246
FEATURE [Part::Box] Box251  label="Re-level Edge Clip Block016"
  AttacherType = Attacher::AttachEngine3D
  Height = 10
  Length = 12
  Placement = pos=(-21.5,-2,-7) rot=(0,0,1;0rad)
  Width = 44
FEATURE [Part::Box] Box252  label="Cube213"
  AttacherType = Attacher::AttachEngine3D
  Height = 7
  Length = 10
  Placement = pos=(-15,10,-2) rot=(0,0,1;0rad)
  Width = 2
FEATURE [Part::Box] Box253  label="Cube214"
  AttacherType = Attacher::AttachEngine3D
  Height = 7
  Length = 4
  Placement = pos=(-6,12,-2) rot=(0,0,1;0rad)
  Width = 1
FEATURE [Part::Box] Box254  label="Chamfer Cube008"
  AttacherType = Attacher::AttachEngine3D
  Height = 10
  Length = 13
  Placement = pos=(-11.69,0,-1.19) rot=(0,-1,0;0.785398rad)
  Width = 40
FEATURE [Part::Sphere] Sphere079
  Angle1 = -90
  Angle2 = 90
  Angle3 = 360
  AttacherType = Attacher::AttachEngine3D
  Placement = pos=(-7.5,6.5,0.5) rot=(0,0,1;0rad)
  Radius = 1.25
FEATURE [Part::Box] Box255  label="Cube215"
  AttacherType = Attacher::AttachEngine3D
  Height = 7
  Length = 5
  Placement = pos=(-5,0,-2) rot=(0,0,1;0rad)
  Width = 40
FEATURE [Part::Box] Box256  label="Cube216"
  AttacherType = Attacher::AttachEngine3D
  Height = 7
  Length = 4
  Placement = pos=(-6,27.4,-2) rot=(0,0,1;0rad)
  Width = 7.2
FEATURE [Part::Box] Box257  label="Cube217"
  AttacherType = Attacher::AttachEngine3D
  Height = 7
  Length = 4
  Placement = pos=(-6,8,-2) rot=(0,0,1;0rad)
  Width = 2
FEATURE [Part::Box] Box258  label="Cube218"
  AttacherType = Attacher::AttachEngine3D
  Height = 7
  Length = 10
  Placement = pos=(-15,6,-2) rot=(0,0,1;0rad)
  Width = 2
FEATURE [Part::Sphere] Sphere080
  Angle1 = -90
  Angle2 = 90
  Angle3 = 360
  AttacherType = Attacher::AttachEngine3D
  Placement = pos=(-7.5,28,0.5) rot=(0,0,1;0rad)
  Radius = 1.5
FEATURE [Part::Box] Box259  label="Cube219"
  AttacherType = Attacher::AttachEngine3D
  Height = 7
  Length = 4
  Placement = pos=(-6,5,-2) rot=(0,0,1;0rad)
  Width = 1
FEATURE [Part::Box] Box260  label="Cube220"
  AttacherType = Attacher::AttachEngine3D
  Height = 7
  Length = 4
  Placement = pos=(-6,24.4,-2) rot=(0,0,1;0rad)
  Width = 1
FEATURE [Part::Sphere] Sphere081
  Angle1 = -90
  Angle2 = 90
  Angle3 = 360
  AttacherType = Attacher::AttachEngine3D
  Placement = pos=(-7.5,11.5,0.5) rot=(0,0,1;0rad)
  Radius = 1.25
FEATURE [Part::Box] Box261  label="Re-level Edge Clip Block017"
  AttacherType = Attacher::AttachEngine3D
  Height = 10
  Length = 20
  Placement = pos=(-19,-2,3) rot=(0,0,1;0rad)
  Width = 44
FEATURE [Part::Box] Box262  label="Cube221"
  AttacherType = Attacher::AttachEngine3D
  Height = 7
  Length = 10
  Placement = pos=(-15,34.6,-2) rot=(0,0,1;0rad)
  Width = 2
FEATURE [Part::Box] Box263  label="Cube222"
  AttacherType = Attacher::AttachEngine3D
  Height = 7
  Length = 10
  Placement = pos=(-15,25.4,-2) rot=(0,0,1;0rad)
  Width = 2
FEATURE [Part::MultiFuse] Fusion096
  Shapes = -> [Box255,Box258,Box252,Box263,Box262]
FEATURE [Part::Box] Box264  label="Cube223"
  AttacherType = Attacher::AttachEngine3D
  Height = 7
  Length = 4
  Placement = pos=(-6,36.6,-2) rot=(0,0,1;0rad)
  Width = 1
FEATURE [Part::MultiFuse] Fusion095  label="Extra Holes for Clips008"
  Shapes = -> [Box256,Box253,Box264,Box257,Box260,Box259]
FEATURE [Part::Fuse] Fusion098  label="Bumps008"
  Base = -> Sphere079
  Tool = -> Sphere081
FEATURE [Part::Fuse] Fusion094
  Base = -> Fusion098
  Tool = -> Fusion096
FEATURE [Part::Sphere] Sphere082
  Angle1 = -90
  Angle2 = 90
  Angle3 = 360
  AttacherType = Attacher::AttachEngine3D
  Placement = pos=(-7.5,34,0.5) rot=(0,0,1;0rad)
  Radius = 1.5
FEATURE [Part::Fuse] Fusion097  label="Holes008"
  Base = -> Sphere080
  Tool = -> Sphere082
FEATURE [Part::Cut] Cut101
  Base = -> Fusion094
  Tool = -> Fusion097
FEATURE [Part::Cut] Cut097
  Base = -> Cut101
  Tool = -> Fusion095
FEATURE [Part::Cut] Cut098
  Base = -> Cut097
  Tool = -> Box261
FEATURE [Part::Cut] Cut099
  Base = -> Cut098
  Tool = -> Box251
FEATURE [Part::Cut] Cut100  label="Edge Clips006"
  Base = -> Cut099
  Placement = pos=(0,40,0) rot=(0,0,-1;1.5708rad)
  Tool = -> Box254
FEATURE [Part::Cut] Cut102
  Base = -> Box075
  Tool = -> Fusion047
FEATURE [Part::Box] Box265  label="Cube224"
  AttacherType = Attacher::AttachEngine3D
  Height = 10
  Length = 10
  Placement = pos=(24,-6,1) rot=(0.205904,-0.974848,-0.085288;0.803573rad)
  Width = 15
FEATURE [Part::Box] Box266  label="Cube225"
  AttacherType = Attacher::AttachEngine3D
  Height = 10
  Length = 10
  Placement = pos=(-6,16,1) rot=(-0.273007,-0.419215,-0.865867;1.78566rad)
  Width = 15
FEATURE [Part::Box] Box267  label="Cube226"
  AttacherType = Attacher::AttachEngine3D
  Height = 10
  Length = 10
  Placement = pos=(16,46,1) rot=(0.381439,0.080566,0.920876;3.07487rad)
  Width = 15
FEATURE [Part::Box] Box268  label="Cube227"
  AttacherType = Attacher::AttachEngine3D
  Height = 10
  Length = 10
  Placement = pos=(46,24,1) rot=(0.442189,-0.287968,0.849437;1.66134rad)
  Width = 15
FEATURE [Part::MultiFuse] Fusion099  label="Glue Dents001"
  Shapes = -> [Box265,Box266,Box267,Box268]
FEATURE [Part::MultiFuse] Fusion100
  Shapes = -> [Cut100,Cut086,Cut091,Cut092]
FEATURE [Part::Fuse] Fusion101
  Base = -> Cut102
  Tool = -> Fusion100
FEATURE [Part::Cut] Cut103  label="Nut Plate"
  Base = -> Fusion101
  Tool = -> Fusion099
FEATURE [Drawing::FeatureViewAnnotation] Annotation001
  Font = Sans
  Rotation = 0
  Scale = 7
  Text = 0.5 rejigged whole thing, stopped clips overhang and moved bump and holes back 0.5
  ViewResult = <g transform="translate(14,30) rotate(0)">\n<text id="Annotation001"\n font-family="Sans"\n font-size="7"\n fill="#000000">\n<tspan x="0" dy="1em">0.5 rejigged whole thing, stopped clips overhang and moved bump and holes back 0.5</tspan>\n</text>\n</g>
  Visible = false
  X = 14
  Y = 30
FEATURE [Drawing::FeaturePage] Page
  EditableTexts = AUTHOR NAME | CREATION DATE | SUPERVISOR NAME | CHECK DATE | SCALE | WEIGHT | NUMBER | SHEET | TITLE | SUBTITLE
  Group = -> [Annotation,Annotation001]
  Template = <path>
FEATURE [Part::Cut] Cut104
  Base = -> Cut103
  Tool = -> Chamfer014
FEATURE [Part::Cut] Cut105
  Base = -> Cut104
  Tool = -> Chamfer013
FEATURE [Part::Cut] Cut106  label="Nut Plate001"
  Base = -> Cut105
  Tool = -> Box145
note: 1 file-system path scrubbed to <path> (originals preserved in the JSON sidecar)
